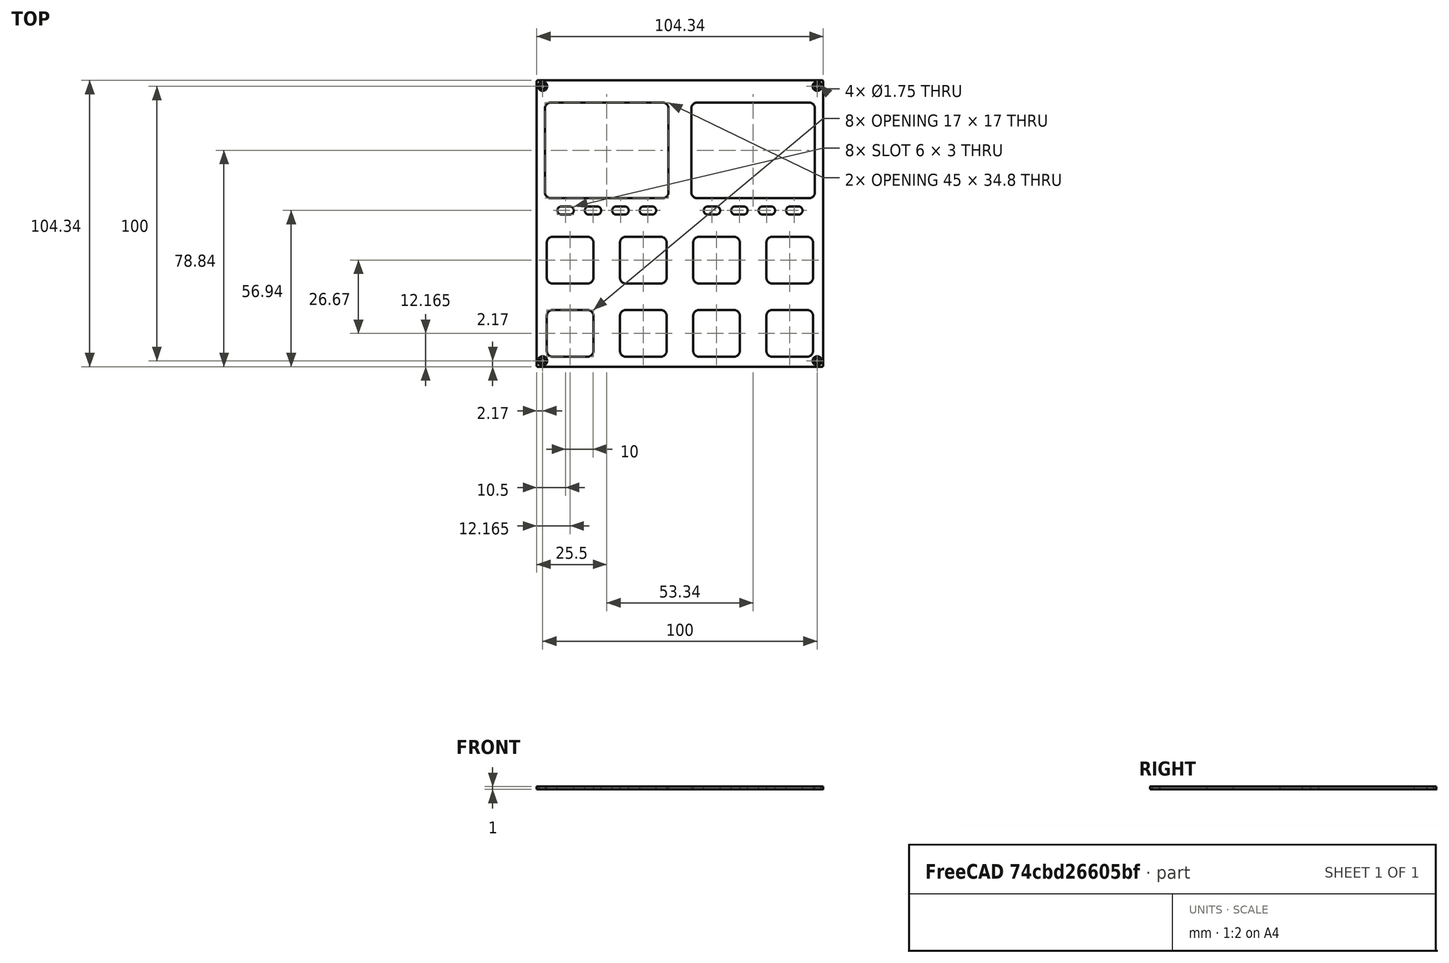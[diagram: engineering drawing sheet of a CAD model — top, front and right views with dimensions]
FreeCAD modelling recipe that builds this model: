
FCSTD DOCUMENT  (FreeCAD 0.21R33771 (Git))
Label: FRONTPANEL-SHEET-VSN2
License: All rights reserved
LicenseURL: https://en.wikipedia.org/wiki/All_rights_reserved
objects: TechDraw::DrawViewDimension×14, Sketcher::SketchObject×11, TechDraw::DrawViewBalloon×11, TechDraw::DrawHatch×11, TechDraw::DrawViewAnnotation×6, TechDraw::DrawViewPart×5, PartDesign::Pocket×4, TechDraw::DrawSVGTemplate×2, PartDesign::Body×2, TechDraw::DrawPage×2, Spreadsheet::Sheet×1, PartDesign::Pad×1, PartDesign::Hole×1, PartDesign::FeatureBase×1, TechDraw::DrawComplexSection×1
note: 47 computed .brp shape members not serialized (recipe doc carries the construction recipe); baked Part::Feature solids carry a one-line shape summary decoded from their .brp

FEATURE [TechDraw::DrawSVGTemplate] Template
  EditableTexts = COLOR=Anodized matte black - RAL code: 9004; CreationDate=2024/08/29; E.G.APPROVED=PRELIMINARY; FC-Scale=1:1; FC-Title=VSN2 - frontpanel; IntechStudioLtd.=Intech Studio Ltd.; MATERIAL=Aluminum 5052-H32; REV=01; STANDARD=ISO 2768 - m
  Height = 297
  Orientation = 1
  Template = <userpath>/Desktop/A3_LandscapeTD_MODIFIED.svg
  Width = 420
FEATURE [Spreadsheet::Sheet] Spreadsheet  label="dim"
  cells = A1='panel_length; B1(panel_length)=104.35; A2='panel_thickness; B2(panel_thickness)=1; A3='panel_radius; B3(panel_radius)==(104.35 - 103.6) / 2; A5='corner_drill_dist; B5(corner_drill_dist)=100; A6='corner_drill_dia; B6(corner_drill_dia)=1.75; A7='corner_drill_countersink; B7(corner_drill_countersink)=3.3; A9='undercut_width; B9(undercut_width)=1; A10='undercut_length; B10(undercut_length)=90; A11='undercut_offset; B11(undercut_offset)=1; A12='undercut_depth; B12(undercut_depth)=0.8; A14='ui_raster; B14(ui_raster)=26.67; A16='light_drill_dia; B16(light_drill_dia)=3; D16='old 2.9; A17='light_bore_dia; B17(light_bore_dia)=3.45; C17='check; D17='old 3.30; E17='DEPRICATED; A18='light_bore_depth; B18(light_bore_depth)=0.4; C18='check; D18='old 0.40; E18='DEPRICATED; A20='pot_drill_dia; B20(pot_drill_dia)=9.8; C20='check; D20='old 6.20; A21='pot_led_dist; B21(pot_led_dist)=8.5; B22=0; A23='but_drill_dia; B23(but_drill_dia)=9.8; A24='but_led_dist; B24(but_led_dist)=8.5; A26='fad_cutout_width; B26(fad_cutout_width)=2.1; C26='check; D26='old 1.50; A27='fad_cutout_length; B27(fad_cutout_length)=36; A28='fad_led_dist; B28(fad_led_dist)=25; A30='enc_drill_dia; B30(enc_drill_dia)=9.8; C30='check; D30='old 6.20; A31='enc_led_dist; B31(enc_led_dist)=8.5; A33='longfad_cutout_width; B33(longfad_cutout_width)=2.1; A34='longfad_cutout_length; B34(longfad_cutout_length)=66; A36='panel_chamfer; B36(panel_chamfer)=0.2; C36='UPDATE DRAWING
FEATURE [Sketcher::SketchObject] Sketch025  label="TEK2_TEKLight"
  FullyConstrained = true
  MapMode = 5
  Support = -> [XY_Plane011]
  expr: Constraints[49] = <<dim>>.light_drill_dia
  sketch-geometry (28):
    g0: Circle CenterX=-26.67 CenterY=26.67 CenterZ=0 NormalX=0 NormalY=0 NormalZ=1 AngleXU=0 Radius=5.25
    g1: Circle CenterX=26.67 CenterY=26.67 CenterZ=0 NormalX=0 NormalY=0 NormalZ=1 AngleXU=0 Radius=5.25
    g2: LineSegment StartX=-26.67 StartY=26.67 StartZ=0 EndX=0 EndY=26.67 EndZ=0
    g3: LineSegment StartX=0 StartY=26.67 StartZ=0 EndX=0 EndY=0 EndZ=0
    g4: LineSegment StartX=26.67 StartY=26.67 StartZ=0 EndX=0 EndY=26.67 EndZ=0
    g5: Circle CenterX=-26.67 CenterY=26.67 CenterZ=0 NormalX=0 NormalY=0 NormalZ=1 AngleXU=0 Radius=23
    g6: Circle CenterX=26.67 CenterY=26.67 CenterZ=0 NormalX=0 NormalY=0 NormalZ=1 AngleXU=0 Radius=23
    g7: Circle CenterX=-47.5151 CenterY=36.3902 CenterZ=0 NormalX=0 NormalY=0 NormalZ=1 AngleXU=0 Radius=1.5
    g8: Circle CenterX=-45.5105 CenterY=39.8623 CenterZ=0 NormalX=0 NormalY=0 NormalZ=1 AngleXU=0 Radius=1.5
    g9: Circle CenterX=-42.9335 CenterY=42.9335 CenterZ=0 NormalX=0 NormalY=0 NormalZ=1 AngleXU=0 Radius=1.5
    g10: Circle CenterX=-39.8623 CenterY=45.5105 CenterZ=0 NormalX=0 NormalY=0 NormalZ=1 AngleXU=0 Radius=1.5
    g11: Circle CenterX=-36.3902 CenterY=47.5151 CenterZ=0 NormalX=0 NormalY=0 NormalZ=1 AngleXU=0 Radius=1.5
    g12: Circle CenterX=5.82492 CenterY=36.3902 CenterZ=0 NormalX=0 NormalY=0 NormalZ=1 AngleXU=0 Radius=1.5
    g13: Circle CenterX=7.8295 CenterY=39.8623 CenterZ=0 NormalX=0 NormalY=0 NormalZ=1 AngleXU=0 Radius=1.5
    g14: Circle CenterX=10.4065 CenterY=42.9335 CenterZ=0 NormalX=0 NormalY=0 NormalZ=1 AngleXU=0 Radius=1.5
    g15: Circle CenterX=13.4777 CenterY=45.5105 CenterZ=0 NormalX=0 NormalY=0 NormalZ=1 AngleXU=0 Radius=1.5
    g16: Circle CenterX=16.9498 CenterY=47.5151 CenterZ=0 NormalX=0 NormalY=0 NormalZ=1 AngleXU=0 Radius=1.5
    g17: LineSegment StartX=-47.5151 StartY=36.3902 StartZ=0 EndX=5.82492 EndY=36.3902 EndZ=0
    g18: LineSegment StartX=-45.5105 StartY=39.8623 StartZ=0 EndX=7.8295 EndY=39.8623 EndZ=0
    g19: LineSegment StartX=-42.9335 StartY=42.9335 StartZ=0 EndX=10.4065 EndY=42.9335 EndZ=0
    g20: LineSegment StartX=-39.8623 StartY=45.5105 StartZ=0 EndX=13.4777 EndY=45.5105 EndZ=0
    g21: LineSegment StartX=-36.3902 StartY=47.5151 StartZ=0 EndX=16.9498 EndY=47.5151 EndZ=0
    g22: LineSegment StartX=5.82492 StartY=36.3902 StartZ=0 EndX=26.67 EndY=26.67 EndZ=0
    g23: LineSegment StartX=16.9498 StartY=47.5151 StartZ=0 EndX=26.67 EndY=26.67 EndZ=0
    g24: LineSegment StartX=5.82492 StartY=36.3902 StartZ=0 EndX=7.8295 EndY=39.8623 EndZ=0
    g25: LineSegment StartX=7.8295 StartY=39.8623 StartZ=0 EndX=10.4065 EndY=42.9335 EndZ=0
    g26: LineSegment StartX=13.4777 StartY=45.5105 StartZ=0 EndX=10.4065 EndY=42.9335 EndZ=0
    g27: LineSegment StartX=16.9498 StartY=47.5151 StartZ=0 EndX=13.4777 EndY=45.5105 EndZ=0
  constraints (69):
    c: Coincident(g2,g0)
    c: PointOnObject(g2,g-2)
    c: Coincident(g2,g3)
    c: Coincident(g3,g-1)
    c: Coincident(g4,g1)
    c: Coincident(g4,g2)
    c: Equal(g3,g2)
    c: Equal(g2,g4)
    c: Horizontal(g2)
    c: Horizontal(g4)
    c: DistanceY(g3,g3) = 26.67
    c: Equal(g0,g1)
    c: Coincident(g5,g0)
    c: Coincident(g6,g1)
    c: Equal(g6,g5)
    c: PointOnObject(g7,g5)
    c: PointOnObject(g8,g5)
    c: PointOnObject(g9,g5)
    c: PointOnObject(g10,g5)
    c: PointOnObject(g11,g5)
    c: PointOnObject(g12,g6)
    c: PointOnObject(g13,g6)
    c: PointOnObject(g14,g6)
    c: PointOnObject(g15,g6)
    c: PointOnObject(g16,g6)
    c: Equal(g7,g8)
    c: Equal(g8,g9)
    c: Equal(g9,g10)
    c: Equal(g10,g11)
    c: Equal(g11,g12)
    c: Equal(g12,g13)
    c: Equal(g13,g14)
    c: Equal(g14,g15)
    c: Equal(g15,g16)
    c: Coincident(g17,g7)
    c: Coincident(g17,g12)
    c: Coincident(g18,g8)
    c: Coincident(g18,g13)
    c: Horizontal(g18)
    c: Coincident(g19,g9)
    c: Coincident(g19,g14)
    c: Horizontal(g19)
    c: Coincident(g20,g10)
    c: Coincident(g20,g15)
    c: Horizontal(g20)
    c: Coincident(g21,g11)
    c: Horizontal(g21)
    c: Coincident(g21,g16)
    c: Horizontal(g17)
    c: Diameter(g12) = 3
    c: Coincident(g22,g12)
    c: Coincident(g22,g1)
    c: Coincident(g23,g16)
    c: Coincident(g23,g1)
    c: Angle(g22,g4) = 0.436332
    c: Angle(g-2,g23) = 0.436332
    c: Coincident(g24,g12)
    c: Coincident(g24,g13)
    c: Coincident(g25,g13)
    c: Coincident(g26,g15)
    c: Coincident(g26,g25)
    c: Coincident(g27,g16)
    c: Coincident(g27,g15)
    c: Coincident(g25,g14)
    c: Equal(g24,g25)
    c: Equal(g25,g26)
    c: Equal(g26,g27)
    c: Radius(g6) = 23
    c: Diameter(g1) = 10.5
FEATURE [Sketcher::SketchObject] Sketch024  label="TEK2_ButtonLight"
  FullyConstrained = true
  MapMode = 5
  Support = -> [XY_Plane011]
  expr: Constraints[42] = <<dim>>.but_led_dist
  sketch-geometry (17):
    g0: Circle CenterX=-40.005 CenterY=-4.835 CenterZ=0 NormalX=0 NormalY=0 NormalZ=1 AngleXU=0 Radius=2
    g1: Circle CenterX=-13.335 CenterY=-4.835 CenterZ=0 NormalX=0 NormalY=0 NormalZ=1 AngleXU=0 Radius=2
    g2: LineSegment StartX=-40.005 StartY=-4.835 StartZ=0 EndX=-13.335 EndY=-4.835 EndZ=0
    g3: Circle CenterX=13.335 CenterY=-4.835 CenterZ=0 NormalX=0 NormalY=0 NormalZ=1 AngleXU=0 Radius=2
    g4: LineSegment StartX=-13.335 StartY=-4.835 StartZ=0 EndX=13.335 EndY=-4.835 EndZ=0
    g5: Circle CenterX=40.005 CenterY=-4.835 CenterZ=0 NormalX=0 NormalY=0 NormalZ=1 AngleXU=0 Radius=2
    g6: LineSegment StartX=13.335 StartY=-4.835 StartZ=0 EndX=40.005 EndY=-4.835 EndZ=0
    g7: Circle CenterX=-40.005 CenterY=-31.505 CenterZ=0 NormalX=0 NormalY=0 NormalZ=1 AngleXU=0 Radius=2
    g8: LineSegment StartX=-40.005 StartY=-4.835 StartZ=0 EndX=-40.005 EndY=-31.505 EndZ=0
    g9: Circle CenterX=-13.335 CenterY=-31.505 CenterZ=0 NormalX=0 NormalY=0 NormalZ=1 AngleXU=0 Radius=2
    g10: LineSegment StartX=-40.005 StartY=-31.505 StartZ=0 EndX=-13.335 EndY=-31.505 EndZ=0
    g11: Circle CenterX=13.335 CenterY=-31.505 CenterZ=0 NormalX=0 NormalY=0 NormalZ=1 AngleXU=0 Radius=2
    g12: LineSegment StartX=-13.335 StartY=-31.505 StartZ=0 EndX=13.335 EndY=-31.505 EndZ=0
    g13: Circle CenterX=40.005 CenterY=-31.505 CenterZ=0 NormalX=0 NormalY=0 NormalZ=1 AngleXU=0 Radius=2
    g14: LineSegment StartX=13.335 StartY=-31.505 StartZ=0 EndX=40.005 EndY=-31.505 EndZ=0
    g15: LineSegment StartX=-13.335 StartY=-4.835 StartZ=0 EndX=-1.8e-15 EndY=8.5 EndZ=0
    g16: LineSegment StartX=-1.8e-15 StartY=8.5 StartZ=0 EndX=13.335 EndY=-4.835 EndZ=0
  constraints (43):
    c: Diameter(g0) = 4
    c: Coincident(g0,g2)
    c: Coincident(g1,g2)
    c: Coincident(g1,g4)
    c: Coincident(g3,g4)
    c: Coincident(g3,g6)
    c: Coincident(g5,g6)
    c: Coincident(g0,g8)
    c: Coincident(g7,g8)
    c: Coincident(g7,g10)
    c: Coincident(g9,g10)
    c: Coincident(g9,g12)
    c: Coincident(g11,g12)
    c: Coincident(g11,g14)
    c: Coincident(g13,g14)
    c: Horizontal(g4)
    c: Horizontal(g2)
    c: Horizontal(g6)
    c: Horizontal(g10)
    c: Horizontal(g12)
    c: Horizontal(g14)
    c: Vertical(g8)
    c: Equal(g8,g2)
    c: Equal(g2,g10)
    c: Equal(g10,g12)
    c: Equal(g12,g4)
    c: Equal(g4,g6)
    c: Equal(g6,g14)
    c: DistanceX(g4,g4) = 26.67
    c: Equal(g7,g9)
    c: Equal(g9,g11)
    c: Equal(g11,g13)
    c: Equal(g13,g5)
    c: Equal(g5,g3)
    c: Equal(g3,g1)
    c: Equal(g1,g0)
    c: Coincident(g15,g1)
    c: PointOnObject(g15,g-2)
    c: Coincident(g15,g16)
    c: Coincident(g16,g3)
    c: Equal(g16,g15)
    c: Perpendicular(g15,g16)
    c: DistanceY(g-1,g15) = 8.5
FEATURE [Sketcher::SketchObject] Sketch023  label="TEK2_ButtonHole"
  FullyConstrained = true
  MapMode = 5
  Support = -> [XY_Plane011]
  sketch-geometry (17):
    g0: Circle CenterX=-40.005 CenterY=-13.335 CenterZ=0 NormalX=0 NormalY=0 NormalZ=1 AngleXU=0 Radius=2
    g1: Circle CenterX=-13.335 CenterY=-13.335 CenterZ=0 NormalX=0 NormalY=0 NormalZ=1 AngleXU=0 Radius=2
    g2: LineSegment StartX=-40.005 StartY=-13.335 StartZ=0 EndX=-13.335 EndY=-13.335 EndZ=0
    g3: Circle CenterX=13.335 CenterY=-13.335 CenterZ=0 NormalX=0 NormalY=0 NormalZ=1 AngleXU=0 Radius=2
    g4: LineSegment StartX=-13.335 StartY=-13.335 StartZ=0 EndX=13.335 EndY=-13.335 EndZ=0
    g5: Circle CenterX=40.005 CenterY=-13.335 CenterZ=0 NormalX=0 NormalY=0 NormalZ=1 AngleXU=0 Radius=2
    g6: LineSegment StartX=13.335 StartY=-13.335 StartZ=0 EndX=40.005 EndY=-13.335 EndZ=0
    g7: Circle CenterX=-40.005 CenterY=-40.005 CenterZ=0 NormalX=0 NormalY=0 NormalZ=1 AngleXU=0 Radius=2
    g8: LineSegment StartX=-40.005 StartY=-13.335 StartZ=0 EndX=-40.005 EndY=-40.005 EndZ=0
    g9: Circle CenterX=-13.335 CenterY=-40.005 CenterZ=0 NormalX=0 NormalY=0 NormalZ=1 AngleXU=0 Radius=2
    g10: LineSegment StartX=-40.005 StartY=-40.005 StartZ=0 EndX=-13.335 EndY=-40.005 EndZ=0
    g11: Circle CenterX=13.335 CenterY=-40.005 CenterZ=0 NormalX=0 NormalY=0 NormalZ=1 AngleXU=0 Radius=2
    g12: LineSegment StartX=-13.335 StartY=-40.005 StartZ=0 EndX=13.335 EndY=-40.005 EndZ=0
    g13: Circle CenterX=40.005 CenterY=-40.005 CenterZ=0 NormalX=0 NormalY=0 NormalZ=1 AngleXU=0 Radius=2
    g14: LineSegment StartX=13.335 StartY=-40.005 StartZ=0 EndX=40.005 EndY=-40.005 EndZ=0
    g15: LineSegment StartX=0 StartY=0 StartZ=0 EndX=13.335 EndY=-13.335 EndZ=0
    g16: LineSegment StartX=0 StartY=0 StartZ=0 EndX=-13.335 EndY=-13.335 EndZ=0
  constraints (42):
    c: Diameter(g0) = 4
    c: Coincident(g0,g2)
    c: Coincident(g1,g2)
    c: Coincident(g1,g4)
    c: Coincident(g3,g4)
    c: Coincident(g3,g6)
    c: Coincident(g5,g6)
    c: Coincident(g0,g8)
    c: Coincident(g7,g8)
    c: Coincident(g7,g10)
    c: Coincident(g9,g10)
    c: Coincident(g9,g12)
    c: Coincident(g11,g12)
    c: Coincident(g11,g14)
    c: Coincident(g13,g14)
    c: Coincident(g-1,g16)
    c: Coincident(g16,g1)
    c: Coincident(g15,g3)
    c: Horizontal(g4)
    c: Horizontal(g2)
    c: Horizontal(g6)
    c: Horizontal(g10)
    c: Horizontal(g12)
    c: Horizontal(g14)
    c: Vertical(g8)
    c: Equal(g8,g2)
    c: Equal(g2,g10)
    c: Equal(g10,g12)
    c: Equal(g12,g4)
    c: Equal(g4,g6)
    c: Equal(g6,g14)
    c: DistanceX(g4,g4) = 26.67
    c: Equal(g16,g15)
    c: Coincident(g15,g16)
    c: Perpendicular(g15,g16)
    c: Equal(g7,g9)
    c: Equal(g9,g11)
    c: Equal(g11,g13)
    c: Equal(g13,g5)
    c: Equal(g5,g3)
    c: Equal(g3,g1)
    c: Equal(g1,g0)
FEATURE [Sketcher::SketchObject] Sketch001
  FullyConstrained = true
  MapMode = 5
  Support = -> [XY_Plane]
  expr: Constraints[13] = <<dim>>.corner_drill_dist
  sketch-geometry (9):
    g0: LineSegment StartX=-50 StartY=50 StartZ=0 EndX=-50 EndY=-50 EndZ=0
    g1: LineSegment StartX=-50 StartY=-50 StartZ=0 EndX=50 EndY=-50 EndZ=0
    g2: LineSegment StartX=50 StartY=-50 StartZ=0 EndX=50 EndY=50 EndZ=0
    g3: LineSegment StartX=50 StartY=50 StartZ=0 EndX=-50 EndY=50 EndZ=0
    g4: Circle CenterX=0 CenterY=0 CenterZ=0 NormalX=0 NormalY=0 NormalZ=1 AngleXU=0 Radius=70.7107
    g5: Circle CenterX=-50 CenterY=50 CenterZ=0 NormalX=0 NormalY=0 NormalZ=1 AngleXU=0 Radius=0.5
    g6: Circle CenterX=50 CenterY=50 CenterZ=0 NormalX=0 NormalY=0 NormalZ=1 AngleXU=0 Radius=0.5
    g7: Circle CenterX=50 CenterY=-50 CenterZ=0 NormalX=0 NormalY=0 NormalZ=1 AngleXU=0 Radius=0.5
    g8: Circle CenterX=-50 CenterY=-50 CenterZ=0 NormalX=0 NormalY=0 NormalZ=1 AngleXU=0 Radius=0.5
  constraints (22):
    c: Coincident(g0,g1)
    c: Coincident(g1,g2)
    c: Coincident(g2,g3)
    c: Coincident(g3,g0)
    c: Equal(g0,g1)
    c: Equal(g0,g2)
    c: Equal(g0,g3)
    c: PointOnObject(g0,g4)
    c: PointOnObject(g1,g4)
    c: PointOnObject(g2,g4)
    c: PointOnObject(g3,g4)
    c: Coincident(g4,g-1)
    c: Horizontal(g3)
    c: DistanceX(g3,g3) = 100
    c: Coincident(g5,g0)
    c: Coincident(g6,g2)
    c: Coincident(g7,g1)
    c: Coincident(g8,g0)
    c: Diameter(g8) = 1
    c: Equal(g8,g7)
    c: Equal(g8,g6)
    c: Equal(g8,g5)
FEATURE [Sketcher::SketchObject] Sketch002
  AttachmentOffset = pos=(0,0,-4.8) rot=(0,0,1;0rad)
  FullyConstrained = true
  MapMode = 5
  Placement = pos=(0,0,-4.8) rot=(0,0,1;0rad)
  Support = -> [XY_Plane]
  expr: .AttachmentOffset.Base.z = -<<dim>>.undercut_depth - 4
  expr: Constraints[91] = <<dim>>.undercut_length
  expr: Constraints[92] = <<dim>>.undercut_width
  expr: Constraints[93] = <<dim>>.panel_length / 2 - <<dim>>.undercut_offset - <<dim>>.undercut_width / 2
  sketch-geometry (40):
    g0: LineSegment StartX=-45 StartY=50.175 StartZ=0 EndX=45 EndY=50.175 EndZ=0
    g1: LineSegment StartX=-45 StartY=51.175 StartZ=0 EndX=45 EndY=51.175 EndZ=0
    g2: LineSegment StartX=-50.675 StartY=45 StartZ=0 EndX=0 EndY=0 EndZ=0
    g3: LineSegment StartX=0 StartY=0 StartZ=0 EndX=-50.675 EndY=-45 EndZ=0
    g4: LineSegment StartX=0 StartY=0 StartZ=0 EndX=-45 EndY=50.675 EndZ=0
    g5: LineSegment StartX=45 StartY=50.675 StartZ=0 EndX=0 EndY=0 EndZ=0
    g6: LineSegment StartX=0 StartY=0 StartZ=0 EndX=50.675 EndY=45 EndZ=0
    g7: LineSegment StartX=50.675 StartY=-45 StartZ=0 EndX=0 EndY=0 EndZ=0
    g8: LineSegment StartX=0 StartY=0 StartZ=0 EndX=45 EndY=-50.675 EndZ=0
    g9: LineSegment StartX=0 StartY=0 StartZ=0 EndX=-45 EndY=-50.675 EndZ=0
    g10: ArcOfCircle CenterX=45 CenterY=50.675 CenterZ=0 NormalX=0 NormalY=0 NormalZ=1 AngleXU=0 Radius=0.5 StartAngle=4.71239 EndAngle=6.28319
    g11: ArcOfCircle CenterX=45 CenterY=50.675 CenterZ=0 NormalX=0 NormalY=0 NormalZ=1 AngleXU=0 Radius=0.5 StartAngle=0 EndAngle=1.5708
    g12: LineSegment StartX=45 StartY=50.675 StartZ=0 EndX=45.5 EndY=50.675 EndZ=0
    g13: ArcOfCircle CenterX=-45 CenterY=50.675 CenterZ=0 NormalX=0 NormalY=0 NormalZ=1 AngleXU=0 Radius=0.5 StartAngle=3.14159 EndAngle=4.71239
    g14: ArcOfCircle CenterX=-45 CenterY=50.675 CenterZ=0 NormalX=0 NormalY=0 NormalZ=1 AngleXU=0 Radius=0.5 StartAngle=1.5708 EndAngle=3.14159
    g15: LineSegment StartX=-45.5 StartY=50.675 StartZ=0 EndX=-45 EndY=50.675 EndZ=0
    g16: LineSegment StartX=-45 StartY=-51.175 StartZ=0 EndX=45 EndY=-51.175 EndZ=0
    g17: LineSegment StartX=-45 StartY=-50.175 StartZ=0 EndX=45 EndY=-50.175 EndZ=0
    g18: ArcOfCircle CenterX=45 CenterY=-50.675 CenterZ=0 NormalX=0 NormalY=0 NormalZ=1 AngleXU=0 Radius=0.5 StartAngle=4.71239 EndAngle=6.28319
    g19: ArcOfCircle CenterX=45 CenterY=-50.675 CenterZ=0 NormalX=0 NormalY=0 NormalZ=1 AngleXU=0 Radius=0.5 StartAngle=0 EndAngle=1.5708
    g20: LineSegment StartX=45 StartY=-50.675 StartZ=0 EndX=45.5 EndY=-50.675 EndZ=0
    g21: ArcOfCircle CenterX=-45 CenterY=-50.675 CenterZ=0 NormalX=0 NormalY=0 NormalZ=1 AngleXU=0 Radius=0.5 StartAngle=3.14159 EndAngle=4.71239
    g22: ArcOfCircle CenterX=-45 CenterY=-50.675 CenterZ=0 NormalX=0 NormalY=0 NormalZ=1 AngleXU=0 Radius=0.5 StartAngle=1.5708 EndAngle=3.14159
    g23: LineSegment StartX=-45.5 StartY=-50.675 StartZ=0 EndX=-45 EndY=-50.675 EndZ=0
    g24: LineSegment StartX=51.175 StartY=-45 StartZ=0 EndX=51.175 EndY=45 EndZ=0
    g25: LineSegment StartX=50.175 StartY=-45 StartZ=0 EndX=50.175 EndY=45 EndZ=0
    g26: ArcOfCircle CenterX=50.675 CenterY=45 CenterZ=0 NormalX=0 NormalY=0 NormalZ=1 AngleXU=0 Radius=0.5 StartAngle=3.8e-15 EndAngle=1.5708
    g27: ArcOfCircle CenterX=50.675 CenterY=45 CenterZ=0 NormalX=0 NormalY=0 NormalZ=1 AngleXU=0 Radius=0.5 StartAngle=1.5708 EndAngle=3.14159
    g28: LineSegment StartX=50.675 StartY=45 StartZ=0 EndX=50.675 EndY=45.5 EndZ=0
    g29: ArcOfCircle CenterX=50.675 CenterY=-45 CenterZ=0 NormalX=0 NormalY=0 NormalZ=1 AngleXU=0 Radius=0.5 StartAngle=4.71239 EndAngle=6.28319
    g30: ArcOfCircle CenterX=50.675 CenterY=-45 CenterZ=0 NormalX=0 NormalY=0 NormalZ=1 AngleXU=0 Radius=0.5 StartAngle=3.14159 EndAngle=4.71239
    g31: LineSegment StartX=50.675 StartY=-45.5 StartZ=0 EndX=50.675 EndY=-45 EndZ=0
    g32: LineSegment StartX=-50.175 StartY=-45 StartZ=0 EndX=-50.175 EndY=45 EndZ=0
    g33: LineSegment StartX=-51.175 StartY=-45 StartZ=0 EndX=-51.175 EndY=45 EndZ=0
    g34: ArcOfCircle CenterX=-50.675 CenterY=45 CenterZ=0 NormalX=0 NormalY=0 NormalZ=1 AngleXU=0 Radius=0.5 StartAngle=1.4e-15 EndAngle=1.5708
    g35: ArcOfCircle CenterX=-50.675 CenterY=45 CenterZ=0 NormalX=0 NormalY=0 NormalZ=1 AngleXU=0 Radius=0.5 StartAngle=1.5708 EndAngle=3.14159
    g36: LineSegment StartX=-50.675 StartY=45 StartZ=0 EndX=-50.675 EndY=45.5 EndZ=0
    g37: ArcOfCircle CenterX=-50.675 CenterY=-45 CenterZ=0 NormalX=0 NormalY=0 NormalZ=1 AngleXU=0 Radius=0.5 StartAngle=4.71239 EndAngle=6.28319
    g38: ArcOfCircle CenterX=-50.675 CenterY=-45 CenterZ=0 NormalX=0 NormalY=0 NormalZ=1 AngleXU=0 Radius=0.5 StartAngle=3.14159 EndAngle=4.71239
    g39: LineSegment StartX=-50.675 StartY=-45.5 StartZ=0 EndX=-50.675 EndY=-45 EndZ=0
  constraints (96):
    c: Horizontal(g0)
    c: Coincident(g2,g-1)
    c: Coincident(g2,g3)
    c: Coincident(g-1,g4)
    c: Coincident(g5,g-1)
    c: Coincident(g5,g6)
    c: Coincident(g7,g-1)
    c: Coincident(g7,g8)
    c: Coincident(g-1,g9)
    c: Equal(g5,g6)
    c: Equal(g6,g8)
    c: Equal(g8,g7)
    c: Equal(g7,g9)
    c: Equal(g9,g3)
    c: Equal(g3,g2)
    c: Equal(g2,g4)
    c: Coincident(g10,g5)
    c: Coincident(g11,g10)
    c: Coincident(g11,g10)
    c: Tangent(g11,g1) = 1.5708
    c: Tangent(g10,g0) = -1.5708
    c: Coincident(g12,g10)
    c: Coincident(g12,g10)
    c: Horizontal(g12)
    c: Coincident(g13,g4)
    c: Coincident(g14,g13)
    c: Coincident(g14,g13)
    c: Tangent(g14,g1) = 1.5708
    c: Tangent(g13,g0) = -1.5708
    c: Coincident(g15,g13)
    c: Coincident(g15,g13)
    c: Horizontal(g15)
    c: Horizontal(g1)
    c: Horizontal(g16)
    c: Coincident(g19,g18)
    c: Coincident(g19,g18)
    c: Tangent(g19,g17) = 1.5708
    c: Tangent(g18,g16) = -1.5708
    c: Coincident(g20,g18)
    c: Coincident(g20,g18)
    c: Horizontal(g20)
    c: Coincident(g22,g21)
    c: Coincident(g22,g21)
    c: Tangent(g22,g17) = 1.5708
    c: Tangent(g21,g16) = -1.5708
    c: Coincident(g23,g21)
    c: Coincident(g23,g21)
    c: Horizontal(g23)
    c: Horizontal(g17)
    c: Coincident(g21,g9)
    c: Coincident(g8,g18)
    c: Equal(g22,g14)
    c: Equal(g17,g1)
    c: Coincident(g27,g26)
    c: Coincident(g27,g26)
    c: Tangent(g27,g25) = 1.5708
    c: Tangent(g26,g24) = -1.5708
    c: Coincident(g28,g26)
    c: Coincident(g28,g26)
    c: Coincident(g30,g29)
    c: Coincident(g30,g29)
    c: Tangent(g30,g25) = 1.5708
    c: Tangent(g29,g24) = -1.5708
    c: Coincident(g31,g29)
    c: Coincident(g31,g29)
    c: Vertical(g31)
    c: Vertical(g28)
    c: Vertical(g25)
    c: Vertical(g24)
    c: Coincident(g35,g34)
    c: Coincident(g35,g34)
    c: Tangent(g35,g33) = 1.5708
    c: Tangent(g34,g32) = -1.5708
    c: Coincident(g36,g34)
    c: Coincident(g36,g34)
    c: Coincident(g38,g37)
    c: Coincident(g38,g37)
    c: Tangent(g38,g33) = 1.5708
    c: Tangent(g37,g32) = -1.5708
    c: Coincident(g39,g37)
    c: Coincident(g39,g37)
    c: Vertical(g39)
    c: Vertical(g36)
    c: Vertical(g33)
    c: Vertical(g32)
    c: Coincident(g6,g26)
    c: Coincident(g7,g29)
    c: Equal(g25,g0)
    c: Equal(g11,g27)
    c: Equal(g1,g33)
    c: Equal(g35,g11)
    c: DistanceX(g13,g10) = 90
    c: Diameter(g13) = 1
    c: DistanceY(g-1,g13) = 50.675
    c: Coincident(g2,g34)
    c: Coincident(g3,g37)
FEATURE [Sketcher::SketchObject] Sketch
  FullyConstrained = true
  MapMode = 5
  Support = -> [XY_Plane]
  expr: Constraints[12] = <<dim>>.panel_radius
  expr: Constraints[16] = <<dim>>.panel_length
  sketch-geometry (11):
    g0: LineSegment StartX=-51.8 StartY=52.175 StartZ=0 EndX=51.8 EndY=52.175 EndZ=0
    g1: LineSegment StartX=52.175 StartY=51.8 StartZ=0 EndX=52.175 EndY=-51.8 EndZ=0
    g2: LineSegment StartX=51.8 StartY=-52.175 StartZ=0 EndX=-51.8 EndY=-52.175 EndZ=0
    g3: LineSegment StartX=-52.175 StartY=-51.8 StartZ=0 EndX=-52.175 EndY=51.8 EndZ=0
    g4: ArcOfCircle CenterX=-51.8 CenterY=51.8 CenterZ=0 NormalX=0 NormalY=0 NormalZ=1 AngleXU=0 Radius=0.375 StartAngle=1.5708 EndAngle=3.14159
    g5: ArcOfCircle CenterX=51.8 CenterY=51.8 CenterZ=0 NormalX=0 NormalY=0 NormalZ=1 AngleXU=0 Radius=0.375 StartAngle=8.4e-15 EndAngle=1.5708
    g6: ArcOfCircle CenterX=51.8 CenterY=-51.8 CenterZ=0 NormalX=0 NormalY=0 NormalZ=1 AngleXU=0 Radius=0.375 StartAngle=4.71239 EndAngle=6.28319
    g7: ArcOfCircle CenterX=-51.8 CenterY=-51.8 CenterZ=0 NormalX=0 NormalY=0 NormalZ=1 AngleXU=0 Radius=0.375 StartAngle=3.14159 EndAngle=4.71239
    g8: LineSegment StartX=-51.8 StartY=51.8 StartZ=0 EndX=0 EndY=0 EndZ=0
    g9: LineSegment StartX=0 StartY=0 StartZ=0 EndX=51.8 EndY=51.8 EndZ=0
    g10: LineSegment StartX=0 StartY=0 StartZ=0 EndX=-51.8 EndY=-51.8 EndZ=0
  constraints (26):
    c: Horizontal(g0)
    c: Horizontal(g2)
    c: Vertical(g1)
    c: Vertical(g3)
    c: Tangent(g3,g4) = 1.5708
    c: Tangent(g0,g4) = 1.5708
    c: Tangent(g0,g5) = 1.5708
    c: Tangent(g1,g5) = 1.5708
    c: Tangent(g1,g6) = 1.5708
    c: Tangent(g2,g6) = 1.5708
    c: Tangent(g2,g7) = 1.5708
    c: Tangent(g3,g7) = 1.5708
    c: Radius(g4) = 0.375
    c: Equal(g4,g5)
    c: Equal(g4,g6)
    c: Equal(g4,g7)
    c: DistanceX(g3,g1) = 104.35
    c: Equal(g3,g0)
    c: Coincident(g8,g4)
    c: Coincident(g8,g-1)
    c: Coincident(g8,g9)
    c: Coincident(g9,g5)
    c: Coincident(g-1,g10)
    c: Coincident(g10,g7)
    c: Equal(g10,g8)
    c: Equal(g8,g9)
FEATURE [PartDesign::Pad] Pad  label="panel"
  AllowMultiFace = false
  Direction = (0,0,1)
  Length = 1
  Length2 = 100
  Profile = -> Sketch
  Reversed = true
  Type = 0
  expr: Length = <<dim>>.panel_thickness
FEATURE [PartDesign::Pocket] Pocket
  AllowMultiFace = false
  BaseFeature = -> Pad
  Direction = (0,0,-1)
  Length = 5
  Length2 = 100
  Profile = -> Sketch002
  Type = 1
FEATURE [PartDesign::Hole] Hole
  BaseFeature = -> Pocket
  CustomThreadClearance = 0
  Depth = 298.105
  DepthType = 1
  Diameter = 1.75
  DrillForDepth = false
  DrillPoint = 1
  DrillPointAngle = 118
  HoleCutCountersinkAngle = 90
  HoleCutCustomValues = false
  HoleCutDepth = 0
  HoleCutDiameter = 3.3
  HoleCutType = 2
  ModelThread = false
  Profile = -> Sketch001
  Tapered = false
  TaperedAngle = 90
  ThreadClass = 0
  ThreadDepth = 298.105
  ThreadDepthType = 0
  ThreadDirection = 0
  ThreadFit = 0
  ThreadSize = 0
  ThreadType = 0
  Threaded = false
  UseCustomThreadClearance = false
  expr: Diameter = <<dim>>.corner_drill_dia
  expr: HoleCutDiameter = <<dim>>.corner_drill_countersink
FEATURE [PartDesign::Body] Body  label="Base"
  Group = -> [Sketch,Pad,Sketch001,Sketch002,Pocket,Hole]
  Origin = -> Origin
  Tip = -> Hole
FEATURE [PartDesign::FeatureBase] Clone009
  BaseFeature = -> Body
FEATURE [Sketcher::SketchObject] Sketch026  label="Section A-A"
  FullyConstrained = true
  MapMode = 5
  Support = -> [XY_Plane011]
  sketch-geometry (1):
    g0: LineSegment StartX=-53.5 StartY=-50 StartZ=0 EndX=-46.5 EndY=-50 EndZ=0
  constraints (4):
    c: Horizontal(g0)
    c: DistanceX(g0,g0) = 7
    c: DistanceY(g0,g-1) = 50
    c: DistanceX(g0,g-1) = 46.5
FEATURE [TechDraw::DrawViewAnnotation] Annotation
  Font = osifont
  LineSpace = 100
  LockPosition = false
  MaxWidth = -1
  Rotation = 0
  ScaleType = 0
  Text = 10:1
  TextSize = 4
  TextStyle = 0
  X = 288.818
  Y = 78.3445
FEATURE [TechDraw::DrawViewAnnotation] Annotation001
  Font = osifont
  LineSpace = 100
  LockPosition = false
  MaxWidth = -1
  Rotation = 0
  ScaleType = 0
  Text = 1:2
  TextSize = 4
  TextStyle = 0
  X = 191.608
  Y = 62.7873
FEATURE [Sketcher::SketchObject] Sketch027
  FullyConstrained = false
  MapMode = 5
  Support = -> [XY_Plane011]
  sketch-geometry (20):
    g0: LineSegment StartX=-49.17 StartY=11.27 StartZ=0 EndX=-49.17 EndY=42.07 EndZ=0
    g1: LineSegment StartX=-47.17 StartY=44.07 StartZ=0 EndX=-6.17 EndY=44.07 EndZ=0
    g2: LineSegment StartX=-4.17 StartY=42.07 StartZ=0 EndX=-4.17 EndY=11.27 EndZ=0
    g3: LineSegment StartX=-6.17 StartY=9.27 StartZ=0 EndX=-47.17 EndY=9.27 EndZ=0
    g4: GeomPoint X=-26.67 Y=26.67 Z=0
    g5: ArcOfCircle CenterX=-47.17 CenterY=42.07 CenterZ=0 NormalX=0 NormalY=0 NormalZ=1 AngleXU=0 Radius=2 StartAngle=1.5708 EndAngle=3.14159
    g6: ArcOfCircle CenterX=-6.17 CenterY=42.07 CenterZ=0 NormalX=0 NormalY=0 NormalZ=1 AngleXU=0 Radius=2 StartAngle=-1.8e-15 EndAngle=1.5708
    g7: ArcOfCircle CenterX=-6.17 CenterY=11.27 CenterZ=0 NormalX=0 NormalY=0 NormalZ=1 AngleXU=0 Radius=2 StartAngle=4.71239 EndAngle=6.28319
    g8: ArcOfCircle CenterX=-47.17 CenterY=11.27 CenterZ=0 NormalX=0 NormalY=0 NormalZ=1 AngleXU=0 Radius=2 StartAngle=3.14159 EndAngle=4.71239
    g9: LineSegment StartX=-26.67 StartY=44.07 StartZ=0 EndX=-26.67 EndY=9.27 EndZ=0
    g10: LineSegment StartX=-49.17 StartY=26.67 StartZ=0 EndX=-4.17 EndY=26.67 EndZ=0
    g11: LineSegment StartX=4.17 StartY=11.27 StartZ=0 EndX=4.17 EndY=42.07 EndZ=0
    g12: LineSegment StartX=6.17 StartY=44.07 StartZ=0 EndX=47.17 EndY=44.07 EndZ=0
    g13: LineSegment StartX=49.17 StartY=42.07 StartZ=0 EndX=49.17 EndY=11.27 EndZ=0
    g14: LineSegment StartX=47.17 StartY=9.27 StartZ=0 EndX=6.17 EndY=9.27 EndZ=0
    g15: GeomPoint X=26.5959 Y=26.67 Z=0
    g16: ArcOfCircle CenterX=6.17 CenterY=42.07 CenterZ=0 NormalX=0 NormalY=0 NormalZ=1 AngleXU=0 Radius=2 StartAngle=1.5708 EndAngle=3.14159
    g17: ArcOfCircle CenterX=47.17 CenterY=42.07 CenterZ=0 NormalX=0 NormalY=0 NormalZ=1 AngleXU=0 Radius=2 StartAngle=-9e-16 EndAngle=1.5708
    g18: ArcOfCircle CenterX=47.17 CenterY=11.27 CenterZ=0 NormalX=0 NormalY=0 NormalZ=1 AngleXU=0 Radius=2 StartAngle=4.71239 EndAngle=6.28319
    g19: ArcOfCircle CenterX=6.17 CenterY=11.27 CenterZ=0 NormalX=0 NormalY=0 NormalZ=1 AngleXU=0 Radius=2 StartAngle=3.14159 EndAngle=4.71239
  constraints (49):
    c: Horizontal(g1)
    c: Horizontal(g3)
    c: Vertical(g0)
    c: Vertical(g2)
    c: DistanceY(g-1,g4) = 26.67
    c: Tangent(g1,g5) = 1.5708
    c: Tangent(g0,g5) = 1.5708
    c: Tangent(g1,g6) = 1.5708
    c: Tangent(g2,g6) = 1.5708
    c: Tangent(g2,g7) = 1.5708
    c: Tangent(g3,g7) = 1.5708
    c: Tangent(g3,g8) = 1.5708
    c: Tangent(g0,g8) = 1.5708
    c: Equal(g5,g6)
    c: Equal(g6,g7)
    c: Equal(g7,g8)
    c: DistanceX(g0,g2) = 45
    c: DistanceY(g3,g1) = 34.8
    c: PointOnObject(g9,g3)
    c: Vertical(g9)
    c: PointOnObject(g10,g0)
    c: Horizontal(g10)
    c: Symmetric(g2,g2,g10)
    c: Symmetric(g1,g1,g9)
    c: PointOnObject(g4,g9)
    c: PointOnObject(g4,g10)
    c: Diameter(g6) = 4
    c: DistanceX(g4,g-1) = 26.67
    c: DistanceY(g-1,g3) = 9.27
    c: Horizontal(g12)
    c: Horizontal(g14)
    c: Vertical(g11)
    c: Vertical(g13)
    c: Horizontal(g15,g4)
    c: Tangent(g12,g16) = 1.5708
    c: Tangent(g11,g16) = 1.5708
    c: Tangent(g12,g17) = 1.5708
    c: Tangent(g13,g17) = 1.5708
    c: Tangent(g13,g18) = 1.5708
    c: Tangent(g14,g18) = 1.5708
    c: Tangent(g11,g19) = 1.5708
    c: Tangent(g14,g19) = 1.5708
    c: Equal(g16,g17)
    c: Equal(g17,g18)
    c: Equal(g18,g19)
    c: Equal(g19,g7)
    c: Equal(g11,g2)
    c: Symmetric(g3,g14,g-2)
    c: Equal(g14,g3)
FEATURE [PartDesign::Pocket] Pocket008  label="TEK1_display"
  BaseFeature = -> Clone009
  Direction = (0,0,-1)
  Length = 5
  Length2 = 5
  Profile = -> Sketch027
  ReferenceAxis = -> Sketch027 [N_Axis]
  Type = 1
FEATURE [Sketcher::SketchObject] Sketch028  label="LocatorPin"
  FullyConstrained = true
  MapMode = 5
  Support = -> [XY_Plane011]
  sketch-geometry (3):
    g0: Circle CenterX=-48.77 CenterY=8.17 CenterZ=0 NormalX=0 NormalY=0 NormalZ=1 AngleXU=0 Radius=0.6
    g1: Circle CenterX=-4.57 CenterY=45.17 CenterZ=0 NormalX=0 NormalY=0 NormalZ=1 AngleXU=0 Radius=0.6
    g2: GeomPoint X=-26.67 Y=26.67 Z=0
  constraints (8):
    c: Equal(g1,g0)
    c: Diameter(g1) = 1.2
    c: DistanceX(g2,g-1) = 26.67
    c: DistanceY(g-1,g2) = 26.67
    c: DistanceX(g0,g2) = 22.1
    c: DistanceY(g0,g2) = 18.5
    c: DistanceX(g2,g1) = 22.1
    c: DistanceY(g2,g1) = 18.5
FEATURE [Sketcher::SketchObject] Sketch029
  FullyConstrained = true
  MapMode = 5
  Support = -> [XY_Plane011]
  sketch-geometry (61):
    g0: LineSegment StartX=-47.07 StartY=4.77 StartZ=0 EndX=-6.27 EndY=4.77 EndZ=0
    g1: GeomPoint X=-26.67 Y=4.77 Z=0
    g2: LineSegment StartX=-34.67 StartY=3.12 StartZ=0 EndX=-34.67 EndY=6.42 EndZ=0
    g3: LineSegment StartX=-34.67 StartY=6.42 StartZ=0 EndX=-28.67 EndY=6.42 EndZ=0
    g4: LineSegment StartX=-28.67 StartY=6.42 StartZ=0 EndX=-28.67 EndY=3.12 EndZ=0
    g5: LineSegment StartX=-28.67 StartY=3.12 StartZ=0 EndX=-34.67 EndY=3.12 EndZ=0
    g6: GeomPoint X=-31.67 Y=4.77 Z=0
    g7: LineSegment StartX=-44.67 StartY=3.12 StartZ=0 EndX=-44.67 EndY=6.42 EndZ=0
    g8: LineSegment StartX=-44.67 StartY=6.42 StartZ=0 EndX=-38.67 EndY=6.42 EndZ=0
    g9: LineSegment StartX=-38.67 StartY=6.42 StartZ=0 EndX=-38.67 EndY=3.12 EndZ=0
    g10: LineSegment StartX=-38.67 StartY=3.12 StartZ=0 EndX=-44.67 EndY=3.12 EndZ=0
    g11: GeomPoint X=-41.67 Y=4.77 Z=0
    g12: LineSegment StartX=-24.67 StartY=3.12 StartZ=0 EndX=-24.67 EndY=6.42 EndZ=0
    g13: LineSegment StartX=-24.67 StartY=6.42 StartZ=0 EndX=-18.67 EndY=6.42 EndZ=0
    g14: LineSegment StartX=-18.67 StartY=6.42 StartZ=0 EndX=-18.67 EndY=3.12 EndZ=0
    g15: LineSegment StartX=-18.67 StartY=3.12 StartZ=0 EndX=-24.67 EndY=3.12 EndZ=0
    g16: GeomPoint X=-21.67 Y=4.77 Z=0
    g17: LineSegment StartX=-14.67 StartY=3.12 StartZ=0 EndX=-14.67 EndY=6.42 EndZ=0
    g18: LineSegment StartX=-14.67 StartY=6.42 StartZ=0 EndX=-8.67 EndY=6.42 EndZ=0
    g19: LineSegment StartX=-8.67 StartY=6.42 StartZ=0 EndX=-8.67 EndY=3.12 EndZ=0
    g20: LineSegment StartX=-8.67 StartY=3.12 StartZ=0 EndX=-14.67 EndY=3.12 EndZ=0
    g21: GeomPoint X=-11.67 Y=4.77 Z=0
    g22: ArcOfCircle CenterX=-33.17 CenterY=4.77 CenterZ=0 NormalX=0 NormalY=0 NormalZ=1 AngleXU=0 Radius=1.5 StartAngle=1.5708 EndAngle=4.71239
    g23: ArcOfCircle CenterX=-30.17 CenterY=4.77 CenterZ=0 NormalX=0 NormalY=0 NormalZ=1 AngleXU=0 Radius=1.5 StartAngle=4.71239 EndAngle=7.85398
    g24: LineSegment StartX=-33.17 StartY=3.27 StartZ=0 EndX=-30.17 EndY=3.27 EndZ=0
    g25: LineSegment StartX=-30.17 StartY=6.27 StartZ=0 EndX=-33.17 EndY=6.27 EndZ=0
    g26: ArcOfCircle CenterX=-23.17 CenterY=4.77 CenterZ=0 NormalX=0 NormalY=0 NormalZ=1 AngleXU=0 Radius=1.5 StartAngle=1.5708 EndAngle=4.71239
    g27: ArcOfCircle CenterX=-20.17 CenterY=4.77 CenterZ=0 NormalX=0 NormalY=0 NormalZ=1 AngleXU=0 Radius=1.5 StartAngle=4.71239 EndAngle=7.85398
    g28: LineSegment StartX=-23.17 StartY=3.27 StartZ=0 EndX=-20.17 EndY=3.27 EndZ=0
    g29: LineSegment StartX=-20.17 StartY=6.27 StartZ=0 EndX=-23.17 EndY=6.27 EndZ=0
    g30: ArcOfCircle CenterX=-13.17 CenterY=4.77 CenterZ=0 NormalX=0 NormalY=0 NormalZ=1 AngleXU=0 Radius=1.5 StartAngle=1.5708 EndAngle=4.71239
    g31: ArcOfCircle CenterX=-10.17 CenterY=4.77 CenterZ=0 NormalX=0 NormalY=0 NormalZ=1 AngleXU=0 Radius=1.5 StartAngle=4.71239 EndAngle=7.85398
    g32: LineSegment StartX=-13.17 StartY=3.27 StartZ=0 EndX=-10.17 EndY=3.27 EndZ=0
    g33: LineSegment StartX=-10.17 StartY=6.27 StartZ=0 EndX=-13.17 EndY=6.27 EndZ=0
    g34: ArcOfCircle CenterX=-43.17 CenterY=4.77 CenterZ=0 NormalX=0 NormalY=0 NormalZ=1 AngleXU=0 Radius=1.5 StartAngle=1.5708 EndAngle=4.71239
    g35: ArcOfCircle CenterX=-40.17 CenterY=4.77 CenterZ=0 NormalX=0 NormalY=0 NormalZ=1 AngleXU=0 Radius=1.5 StartAngle=4.71239 EndAngle=7.85398
    g36: LineSegment StartX=-43.17 StartY=3.27 StartZ=0 EndX=-40.17 EndY=3.27 EndZ=0
    g37: LineSegment StartX=-40.17 StartY=6.27 StartZ=0 EndX=-43.17 EndY=6.27 EndZ=0
    g38: GeomPoint X=-26.67 Y=11.37 Z=0
    g39: LineSegment StartX=6.27 StartY=4.77 StartZ=0 EndX=47.07 EndY=4.77 EndZ=0
    g40: ArcOfCircle CenterX=10.17 CenterY=4.77 CenterZ=0 NormalX=0 NormalY=0 NormalZ=1 AngleXU=0 Radius=1.5 StartAngle=1.5708 EndAngle=4.71239
    g41: ArcOfCircle CenterX=13.17 CenterY=4.77 CenterZ=0 NormalX=0 NormalY=0 NormalZ=1 AngleXU=0 Radius=1.5 StartAngle=4.71239 EndAngle=7.85398
    g42: LineSegment StartX=10.17 StartY=3.27 StartZ=0 EndX=13.17 EndY=3.27 EndZ=0
    g43: LineSegment StartX=13.17 StartY=6.27 StartZ=0 EndX=10.17 EndY=6.27 EndZ=0
    g44: ArcOfCircle CenterX=20.17 CenterY=4.77 CenterZ=0 NormalX=0 NormalY=0 NormalZ=1 AngleXU=0 Radius=1.5 StartAngle=1.5708 EndAngle=4.71239
    g45: ArcOfCircle CenterX=23.17 CenterY=4.77 CenterZ=0 NormalX=0 NormalY=0 NormalZ=1 AngleXU=0 Radius=1.5 StartAngle=4.71239 EndAngle=7.85398
    g46: LineSegment StartX=20.17 StartY=3.27 StartZ=0 EndX=23.17 EndY=3.27 EndZ=0
    g47: LineSegment StartX=23.17 StartY=6.27 StartZ=0 EndX=20.17 EndY=6.27 EndZ=0
    g48: ArcOfCircle CenterX=30.17 CenterY=4.77 CenterZ=0 NormalX=0 NormalY=0 NormalZ=1 AngleXU=0 Radius=1.5 StartAngle=1.5708 EndAngle=4.71239
    g49: ArcOfCircle CenterX=33.17 CenterY=4.77 CenterZ=0 NormalX=0 NormalY=0 NormalZ=1 AngleXU=0 Radius=1.5 StartAngle=4.71239 EndAngle=7.85398
    g50: LineSegment StartX=30.17 StartY=3.27 StartZ=0 EndX=33.17 EndY=3.27 EndZ=0
    g51: LineSegment StartX=33.17 StartY=6.27 StartZ=0 EndX=30.17 EndY=6.27 EndZ=0
    g52: ArcOfCircle CenterX=40.17 CenterY=4.77 CenterZ=0 NormalX=0 NormalY=0 NormalZ=1 AngleXU=0 Radius=1.5 StartAngle=1.5708 EndAngle=4.71239
    g53: ArcOfCircle CenterX=43.17 CenterY=4.77 CenterZ=0 NormalX=0 NormalY=0 NormalZ=1 AngleXU=0 Radius=1.5 StartAngle=4.71239 EndAngle=7.85398
    g54: LineSegment StartX=40.17 StartY=3.27 StartZ=0 EndX=43.17 EndY=3.27 EndZ=0
    g55: LineSegment StartX=43.17 StartY=6.27 StartZ=0 EndX=40.17 EndY=6.27 EndZ=0
    g56: GeomPoint X=26.67 Y=4.77 Z=0
    g57: GeomPoint X=11.67 Y=4.77 Z=0
    g58: GeomPoint X=21.67 Y=4.77 Z=0
    g59: GeomPoint X=31.67 Y=4.77 Z=0
    g60: GeomPoint X=41.67 Y=4.77 Z=0
  constraints (140):
    c: Horizontal(g0)
    c: DistanceX(g0,g0) = 40.8
    c: Symmetric(g0,g0,g1)
    c: DistanceX(g1,g-1) = 26.67
    c: Coincident(g2,g3)
    c: Coincident(g3,g4)
    c: Coincident(g4,g5)
    c: Coincident(g5,g2)
    c: Horizontal(g3)
    c: Horizontal(g5)
    c: Vertical(g2)
    c: Vertical(g4)
    c: Symmetric(g3,g2,g6)
    c: PointOnObject(g6,g0)
    c: Coincident(g7,g8)
    c: Coincident(g8,g9)
    c: Coincident(g9,g10)
    c: Coincident(g10,g7)
    c: Horizontal(g8)
    c: Horizontal(g10)
    c: Vertical(g7)
    c: Vertical(g9)
    c: Symmetric(g8,g7,g11)
    c: PointOnObject(g11,g0)
    c: Coincident(g12,g13)
    c: Coincident(g13,g14)
    c: Coincident(g14,g15)
    c: Coincident(g15,g12)
    c: Horizontal(g13)
    c: Horizontal(g15)
    c: Vertical(g12)
    c: Vertical(g14)
    c: Symmetric(g13,g12,g16)
    c: Coincident(g17,g18)
    c: Coincident(g18,g19)
    c: Coincident(g19,g20)
    c: Coincident(g20,g17)
    c: Horizontal(g18)
    c: Horizontal(g20)
    c: Vertical(g17)
    c: Vertical(g19)
    c: Symmetric(g18,g17,g21)
    c: Symmetric(g16,g6,g1)
    c: Symmetric(g11,g21,g1)
    c: Equal(g13,g3)
    c: Equal(g3,g8)
    c: Equal(g8,g18)
    c: Equal(g14,g17)
    c: Equal(g17,g4)
    c: Equal(g4,g9)
    c: DistanceX(g13,g13) = 6
    c: DistanceY(g19,g19) = 3.3
    c: Tangent(g22,g24) = -1.5708
    c: Tangent(g24,g23) = -1.5708
    c: Tangent(g23,g25) = -1.5708
    c: Tangent(g25,g22) = -1.5708
    c: Equal(g22,g23)
    c: PointOnObject(g22,g0)
    c: Tangent(g26,g28) = -1.5708
    c: Tangent(g28,g27) = -1.5708
    c: Tangent(g27,g29) = -1.5708
    c: Tangent(g29,g26) = -1.5708
    c: Equal(g26,g27)
    c: PointOnObject(g26,g0)
    c: Tangent(g30,g32) = -1.5708
    c: Tangent(g32,g31) = -1.5708
    c: Tangent(g31,g33) = -1.5708
    c: Tangent(g33,g30) = -1.5708
    c: Equal(g30,g31)
    c: PointOnObject(g30,g0)
    c: Tangent(g34,g36) = -1.5708
    c: Tangent(g36,g35) = -1.5708
    c: Tangent(g35,g37) = -1.5708
    c: Tangent(g37,g34) = -1.5708
    c: Equal(g34,g35)
    c: PointOnObject(g34,g0)
    c: Equal(g35,g23)
    c: Equal(g23,g27)
    c: Equal(g27,g31)
    c: Equal(g29,g33)
    c: Equal(g33,g25)
    c: Equal(g25,g37)
    c: Symmetric(g34,g35,g11)
    c: Symmetric(g22,g23,g6)
    c: Symmetric(g26,g27,g16)
    c: Symmetric(g30,g31,g21)
    c: Diameter(g31) = 3
    c: DistanceX(g33,g33) = 3
    c: DistanceY(g-1,g38) = 11.37
    c: Vertical(g38,g1)
    c: DistanceY(g23,g38) = 5.1
    c: DistanceY(g-1,g0) = 4.77
    c: Horizontal(g39)
    c: Tangent(g40,g42) = -1.5708
    c: Tangent(g42,g41) = -1.5708
    c: Tangent(g41,g43) = -1.5708
    c: Tangent(g43,g40) = -1.5708
    c: Equal(g40,g41)
    c: PointOnObject(g40,g39)
    c: PointOnObject(g41,g39)
    c: Tangent(g44,g46) = -1.5708
    c: Tangent(g46,g45) = -1.5708
    c: Tangent(g45,g47) = -1.5708
    c: Tangent(g47,g44) = -1.5708
    c: Equal(g44,g45)
    c: PointOnObject(g44,g39)
    c: PointOnObject(g45,g39)
    c: Tangent(g48,g50) = -1.5708
    c: Tangent(g50,g49) = -1.5708
    c: Tangent(g49,g51) = -1.5708
    c: Tangent(g51,g48) = -1.5708
    c: Equal(g48,g49)
    c: PointOnObject(g48,g39)
    c: Tangent(g52,g54) = -1.5708
    c: Tangent(g54,g53) = -1.5708
    c: Tangent(g53,g55) = -1.5708
    c: Tangent(g55,g52) = -1.5708
    c: Equal(g52,g53)
    c: PointOnObject(g52,g39)
    c: Equal(g31,g40)
    c: Equal(g40,g44)
    c: Equal(g44,g48)
    c: Equal(g48,g52)
    c: Symmetric(g39,g0,g-2)
    c: Equal(g33,g43)
    c: Equal(g43,g47)
    c: Equal(g47,g51)
    c: Equal(g51,g55)
    c: DistanceX(g6,g16) = 10
    c: DistanceX(g16,g21) = 10
    c: Equal(g0,g39)
    c: Symmetric(g39,g39,g56)
    c: Symmetric(g52,g53,g60)
    c: Symmetric(g49,g48,g59)
    c: Symmetric(g44,g45,g58)
    c: Symmetric(g41,g40,g57)
    c: Symmetric(g58,g59,g56)
    c: DistanceX(g58,g59) = 10
    c: DistanceX(g57,g58) = 10
    c: Symmetric(g57,g60,g56)
FEATURE [PartDesign::Pocket] Pocket010  label="TEK1_button"
  BaseFeature = -> Pocket008
  Direction = (0,0,-1)
  Length = 5
  Length2 = 5
  Profile = -> Sketch029
  ReferenceAxis = -> Sketch029 [N_Axis]
  Type = 0
FEATURE [TechDraw::DrawSVGTemplate] Template002
  Height = 210
  Orientation = 1
  Template = C:/Program Files/FreeCAD 0.21/data/Mod/TechDraw/Templates/A4_Landscape_blank.svg
  Width = 297
FEATURE [TechDraw::DrawViewAnnotation] Annotation002
  Font = osifont
  LineSpace = 100
  LockPosition = false
  MaxWidth = -1
  Rotation = 0
  ScaleType = 0
  Text = The mid of the datum plane A is preferred to be near | to the lower limit of the flatness tolerance zone. | It can be achieved with an additional bending step. | Aesthetical surfaces colored red on the view | No scratches, burrs or any kind of damage allowed! | Functional surfaces colored blue on the view (all which perpendicular to the aesthetical) | No burrs or other protruding material allowed!
  TextSize = 3
  TextStyle = 0
  X = 97.2718
  Y = 52.2376
FEATURE [TechDraw::DrawViewAnnotation] Annotation003
  Font = osifont
  LineSpace = 100
  LockPosition = false
  MaxWidth = -1
  Rotation = 0
  ScaleType = 0
  Text = The mid of the datum plane A is preferred to be near | to the lower limit of the flatness tolerance zone. | It can be achieved with an additional bending step.
  TextSize = 4
  TextStyle = 0
  X = 283.844
  Y = 84.5906
FEATURE [Sketcher::SketchObject] Sketch030  label="TEK2_ButtonHole001"
  FullyConstrained = true
  MapMode = 5
  Support = -> [XY_Plane011]
  sketch-geometry (97):
    g0: Circle CenterX=-40.005 CenterY=-13.335 CenterZ=0 NormalX=0 NormalY=0 NormalZ=1 AngleXU=0 Radius=2
    g1: Circle CenterX=-13.335 CenterY=-13.335 CenterZ=0 NormalX=0 NormalY=0 NormalZ=1 AngleXU=0 Radius=2
    g2: LineSegment StartX=-40.005 StartY=-13.335 StartZ=0 EndX=-13.335 EndY=-13.335 EndZ=0
    g3: Circle CenterX=13.335 CenterY=-13.335 CenterZ=0 NormalX=0 NormalY=0 NormalZ=1 AngleXU=0 Radius=2
    g4: LineSegment StartX=-13.335 StartY=-13.335 StartZ=0 EndX=13.335 EndY=-13.335 EndZ=0
    g5: Circle CenterX=40.005 CenterY=-13.335 CenterZ=0 NormalX=0 NormalY=0 NormalZ=1 AngleXU=0 Radius=2
    g6: LineSegment StartX=13.335 StartY=-13.335 StartZ=0 EndX=40.005 EndY=-13.335 EndZ=0
    g7: Circle CenterX=-40.005 CenterY=-40.005 CenterZ=0 NormalX=0 NormalY=0 NormalZ=1 AngleXU=0 Radius=2
    g8: LineSegment StartX=-40.005 StartY=-13.335 StartZ=0 EndX=-40.005 EndY=-40.005 EndZ=0
    g9: Circle CenterX=-13.335 CenterY=-40.005 CenterZ=0 NormalX=0 NormalY=0 NormalZ=1 AngleXU=0 Radius=2
    g10: LineSegment StartX=-40.005 StartY=-40.005 StartZ=0 EndX=-13.335 EndY=-40.005 EndZ=0
    g11: Circle CenterX=13.335 CenterY=-40.005 CenterZ=0 NormalX=0 NormalY=0 NormalZ=1 AngleXU=0 Radius=2
    g12: LineSegment StartX=-13.335 StartY=-40.005 StartZ=0 EndX=13.335 EndY=-40.005 EndZ=0
    g13: Circle CenterX=40.005 CenterY=-40.005 CenterZ=0 NormalX=0 NormalY=0 NormalZ=1 AngleXU=0 Radius=2
    g14: LineSegment StartX=13.335 StartY=-40.005 StartZ=0 EndX=40.005 EndY=-40.005 EndZ=0
    g15: LineSegment StartX=0 StartY=0 StartZ=0 EndX=13.335 EndY=-13.335 EndZ=0
    g16: LineSegment StartX=0 StartY=0 StartZ=0 EndX=-13.335 EndY=-13.335 EndZ=0
    g17: LineSegment StartX=-48.505 StartY=-19.735 StartZ=0 EndX=-48.505 EndY=-6.935 EndZ=0
    g18: LineSegment StartX=-46.405 StartY=-4.835 StartZ=0 EndX=-33.605 EndY=-4.835 EndZ=0
    g19: LineSegment StartX=-31.505 StartY=-6.935 StartZ=0 EndX=-31.505 EndY=-19.735 EndZ=0
    g20: LineSegment StartX=-33.605 StartY=-21.835 StartZ=0 EndX=-46.405 EndY=-21.835 EndZ=0
    g21: GeomPoint X=-40.005 Y=-13.335 Z=0
    g22: LineSegment StartX=-21.835 StartY=-19.735 StartZ=0 EndX=-21.835 EndY=-6.935 EndZ=0
    g23: LineSegment StartX=-19.735 StartY=-4.835 StartZ=0 EndX=-6.935 EndY=-4.835 EndZ=0
    g24: LineSegment StartX=-4.835 StartY=-6.935 StartZ=0 EndX=-4.835 EndY=-19.735 EndZ=0
    g25: LineSegment StartX=-6.935 StartY=-21.835 StartZ=0 EndX=-19.735 EndY=-21.835 EndZ=0
    g26: GeomPoint X=-13.335 Y=-13.335 Z=0
    g27: LineSegment StartX=4.835 StartY=-19.735 StartZ=0 EndX=4.835 EndY=-6.935 EndZ=0
    g28: LineSegment StartX=6.935 StartY=-4.835 StartZ=0 EndX=19.735 EndY=-4.835 EndZ=0
    g29: LineSegment StartX=21.835 StartY=-6.935 StartZ=0 EndX=21.835 EndY=-19.735 EndZ=0
    g30: LineSegment StartX=19.735 StartY=-21.835 StartZ=0 EndX=6.935 EndY=-21.835 EndZ=0
    g31: GeomPoint X=13.335 Y=-13.335 Z=0
    g32: LineSegment StartX=31.505 StartY=-19.735 StartZ=0 EndX=31.505 EndY=-6.935 EndZ=0
    g33: LineSegment StartX=33.605 StartY=-4.835 StartZ=0 EndX=46.405 EndY=-4.835 EndZ=0
    g34: LineSegment StartX=48.505 StartY=-6.935 StartZ=0 EndX=48.505 EndY=-19.735 EndZ=0
    g35: LineSegment StartX=46.405 StartY=-21.835 StartZ=0 EndX=33.605 EndY=-21.835 EndZ=0
    g36: GeomPoint X=40.005 Y=-13.335 Z=0
    g37: LineSegment StartX=31.505 StartY=-46.405 StartZ=0 EndX=31.505 EndY=-33.605 EndZ=0
    g38: LineSegment StartX=33.605 StartY=-31.505 StartZ=0 EndX=46.405 EndY=-31.505 EndZ=0
    g39: LineSegment StartX=48.505 StartY=-33.605 StartZ=0 EndX=48.505 EndY=-46.405 EndZ=0
    g40: LineSegment StartX=46.405 StartY=-48.505 StartZ=0 EndX=33.605 EndY=-48.505 EndZ=0
    g41: GeomPoint X=40.005 Y=-40.005 Z=0
    g42: LineSegment StartX=4.835 StartY=-46.405 StartZ=0 EndX=4.835 EndY=-33.605 EndZ=0
    g43: LineSegment StartX=6.935 StartY=-31.505 StartZ=0 EndX=19.735 EndY=-31.505 EndZ=0
    g44: LineSegment StartX=21.835 StartY=-33.605 StartZ=0 EndX=21.835 EndY=-46.405 EndZ=0
    g45: LineSegment StartX=19.735 StartY=-48.505 StartZ=0 EndX=6.935 EndY=-48.505 EndZ=0
    g46: GeomPoint X=13.335 Y=-40.005 Z=0
    g47: LineSegment StartX=-21.835 StartY=-46.405 StartZ=0 EndX=-21.835 EndY=-33.605 EndZ=0
    g48: LineSegment StartX=-19.735 StartY=-31.505 StartZ=0 EndX=-6.935 EndY=-31.505 EndZ=0
    g49: LineSegment StartX=-4.835 StartY=-33.605 StartZ=0 EndX=-4.835 EndY=-46.405 EndZ=0
    g50: LineSegment StartX=-6.935 StartY=-48.505 StartZ=0 EndX=-19.735 EndY=-48.505 EndZ=0
    g51: GeomPoint X=-13.335 Y=-40.005 Z=0
    g52: LineSegment StartX=-48.505 StartY=-46.405 StartZ=0 EndX=-48.505 EndY=-33.605 EndZ=0
    g53: LineSegment StartX=-46.405 StartY=-31.505 StartZ=0 EndX=-33.605 EndY=-31.505 EndZ=0
    g54: LineSegment StartX=-31.505 StartY=-33.605 StartZ=0 EndX=-31.505 EndY=-46.405 EndZ=0
    g55: LineSegment StartX=-33.605 StartY=-48.505 StartZ=0 EndX=-46.405 EndY=-48.505 EndZ=0
    g56: GeomPoint X=-40.005 Y=-40.005 Z=0
    g57: ArcOfCircle CenterX=-46.405 CenterY=-6.935 CenterZ=0 NormalX=0 NormalY=0 NormalZ=1 AngleXU=0 Radius=2.1 StartAngle=1.5708 EndAngle=3.14159
    g58: ArcOfCircle CenterX=-33.605 CenterY=-6.935 CenterZ=0 NormalX=0 NormalY=0 NormalZ=1 AngleXU=0 Radius=2.1 StartAngle=0 EndAngle=1.5708
    g59: ArcOfCircle CenterX=-33.605 CenterY=-19.735 CenterZ=0 NormalX=0 NormalY=0 NormalZ=1 AngleXU=0 Radius=2.1 StartAngle=4.71239 EndAngle=6.28319
    g60: ArcOfCircle CenterX=-46.405 CenterY=-19.735 CenterZ=0 NormalX=0 NormalY=0 NormalZ=1 AngleXU=0 Radius=2.1 StartAngle=3.14159 EndAngle=4.71239
    g61: ArcOfCircle CenterX=-19.735 CenterY=-6.935 CenterZ=0 NormalX=0 NormalY=0 NormalZ=1 AngleXU=0 Radius=2.1 StartAngle=1.5708 EndAngle=3.14159
    g62: ArcOfCircle CenterX=-19.735 CenterY=-19.735 CenterZ=0 NormalX=0 NormalY=0 NormalZ=1 AngleXU=0 Radius=2.1 StartAngle=3.14159 EndAngle=4.71239
    g63: ArcOfCircle CenterX=-6.935 CenterY=-19.735 CenterZ=0 NormalX=0 NormalY=0 NormalZ=1 AngleXU=0 Radius=2.1 StartAngle=4.71239 EndAngle=6.28319
    g64: ArcOfCircle CenterX=-6.935 CenterY=-6.935 CenterZ=0 NormalX=0 NormalY=0 NormalZ=1 AngleXU=0 Radius=2.1 StartAngle=0 EndAngle=1.5708
    g65: ArcOfCircle CenterX=6.935 CenterY=-6.935 CenterZ=0 NormalX=0 NormalY=0 NormalZ=1 AngleXU=0 Radius=2.1 StartAngle=1.5708 EndAngle=3.14159
    g66: ArcOfCircle CenterX=19.735 CenterY=-6.935 CenterZ=0 NormalX=0 NormalY=0 NormalZ=1 AngleXU=0 Radius=2.1 StartAngle=0 EndAngle=1.5708
    g67: ArcOfCircle CenterX=19.735 CenterY=-19.735 CenterZ=0 NormalX=0 NormalY=0 NormalZ=1 AngleXU=0 Radius=2.1 StartAngle=4.71239 EndAngle=6.28319
    g68: ArcOfCircle CenterX=6.935 CenterY=-19.735 CenterZ=0 NormalX=0 NormalY=0 NormalZ=1 AngleXU=0 Radius=2.1 StartAngle=3.14159 EndAngle=4.71239
    g69: ArcOfCircle CenterX=33.605 CenterY=-19.735 CenterZ=0 NormalX=0 NormalY=0 NormalZ=1 AngleXU=0 Radius=2.1 StartAngle=3.14159 EndAngle=4.71239
    g70: ArcOfCircle CenterX=46.405 CenterY=-6.935 CenterZ=0 NormalX=0 NormalY=0 NormalZ=1 AngleXU=0 Radius=2.1 StartAngle=0 EndAngle=1.5708
    g71: ArcOfCircle CenterX=33.605 CenterY=-6.935 CenterZ=0 NormalX=0 NormalY=0 NormalZ=1 AngleXU=0 Radius=2.1 StartAngle=1.5708 EndAngle=3.14159
    g72: ArcOfCircle CenterX=46.405 CenterY=-19.735 CenterZ=0 NormalX=0 NormalY=0 NormalZ=1 AngleXU=0 Radius=2.1 StartAngle=4.71239 EndAngle=6.28319
    g73: ArcOfCircle CenterX=33.605 CenterY=-33.605 CenterZ=0 NormalX=0 NormalY=0 NormalZ=1 AngleXU=0 Radius=2.1 StartAngle=1.5708 EndAngle=3.14159
    g74: ArcOfCircle CenterX=46.405 CenterY=-46.405 CenterZ=0 NormalX=0 NormalY=0 NormalZ=1 AngleXU=0 Radius=2.1 StartAngle=4.71239 EndAngle=6.28319
    g75: ArcOfCircle CenterX=46.405 CenterY=-33.605 CenterZ=0 NormalX=0 NormalY=0 NormalZ=1 AngleXU=0 Radius=2.1 StartAngle=-9e-16 EndAngle=1.5708
    g76: ArcOfCircle CenterX=33.605 CenterY=-46.405 CenterZ=0 NormalX=0 NormalY=0 NormalZ=1 AngleXU=0 Radius=2.1 StartAngle=3.14159 EndAngle=4.71239
    g77: ArcOfCircle CenterX=6.935 CenterY=-33.605 CenterZ=0 NormalX=0 NormalY=0 NormalZ=1 AngleXU=0 Radius=2.1 StartAngle=1.5708 EndAngle=3.14159
    g78: ArcOfCircle CenterX=19.735 CenterY=-33.605 CenterZ=0 NormalX=0 NormalY=0 NormalZ=1 AngleXU=0 Radius=2.1 StartAngle=-9e-16 EndAngle=1.5708
    g79: ArcOfCircle CenterX=19.735 CenterY=-46.405 CenterZ=0 NormalX=0 NormalY=0 NormalZ=1 AngleXU=0 Radius=2.1 StartAngle=4.71239 EndAngle=6.28319
    g80: ArcOfCircle CenterX=6.935 CenterY=-46.405 CenterZ=0 NormalX=0 NormalY=0 NormalZ=1 AngleXU=0 Radius=2.1 StartAngle=3.14159 EndAngle=4.71239
    g81: ArcOfCircle CenterX=-6.935 CenterY=-33.605 CenterZ=0 NormalX=0 NormalY=0 NormalZ=1 AngleXU=0 Radius=2.1 StartAngle=-1.8e-15 EndAngle=1.5708
    g82: ArcOfCircle CenterX=-19.735 CenterY=-46.405 CenterZ=0 NormalX=0 NormalY=0 NormalZ=1 AngleXU=0 Radius=2.1 StartAngle=3.14159 EndAngle=4.71239
    g83: ArcOfCircle CenterX=-19.735 CenterY=-33.605 CenterZ=0 NormalX=0 NormalY=0 NormalZ=1 AngleXU=0 Radius=2.1 StartAngle=1.5708 EndAngle=3.14159
    g84: ArcOfCircle CenterX=-6.935 CenterY=-46.405 CenterZ=0 NormalX=0 NormalY=0 NormalZ=1 AngleXU=0 Radius=2.1 StartAngle=4.71239 EndAngle=6.28319
    g85: ArcOfCircle CenterX=-46.405 CenterY=-33.605 CenterZ=0 NormalX=0 NormalY=0 NormalZ=1 AngleXU=0 Radius=2.1 StartAngle=1.5708 EndAngle=3.14159
    g86: ArcOfCircle CenterX=-33.605 CenterY=-33.605 CenterZ=0 NormalX=0 NormalY=0 NormalZ=1 AngleXU=0 Radius=2.1 StartAngle=-1.8e-15 EndAngle=1.5708
    g87: ArcOfCircle CenterX=-46.405 CenterY=-46.405 CenterZ=0 NormalX=0 NormalY=0 NormalZ=1 AngleXU=0 Radius=2.1 StartAngle=3.14159 EndAngle=4.71239
    g88: ArcOfCircle CenterX=-33.605 CenterY=-46.405 CenterZ=0 NormalX=0 NormalY=0 NormalZ=1 AngleXU=0 Radius=2.1 StartAngle=4.71239 EndAngle=6.28319
    g89: LineSegment StartX=-40.005 StartY=-4.835 StartZ=0 EndX=-40.005 EndY=-21.835 EndZ=0
    g90: LineSegment StartX=-13.335 StartY=-4.835 StartZ=0 EndX=-13.335 EndY=-21.835 EndZ=0
    g91: LineSegment StartX=13.335 StartY=-4.835 StartZ=0 EndX=13.335 EndY=-21.835 EndZ=0
    g92: LineSegment StartX=40.005 StartY=-4.835 StartZ=0 EndX=40.005 EndY=-21.835 EndZ=0
    g93: LineSegment StartX=40.005 StartY=-31.505 StartZ=0 EndX=40.005 EndY=-48.505 EndZ=0
    g94: LineSegment StartX=13.335 StartY=-31.505 StartZ=0 EndX=13.335 EndY=-48.505 EndZ=0
    g95: LineSegment StartX=-13.335 StartY=-31.505 StartZ=0 EndX=-13.335 EndY=-48.505 EndZ=0
    g96: LineSegment StartX=-40.005 StartY=-31.505 StartZ=0 EndX=-40.005 EndY=-48.505 EndZ=0
  constraints (226):
    c: Diameter(g0) = 4
    c: Coincident(g0,g2)
    c: Coincident(g1,g2)
    c: Coincident(g1,g4)
    c: Coincident(g3,g4)
    c: Coincident(g3,g6)
    c: Coincident(g5,g6)
    c: Coincident(g0,g8)
    c: Coincident(g7,g8)
    c: Coincident(g7,g10)
    c: Coincident(g9,g10)
    c: Coincident(g9,g12)
    c: Coincident(g11,g12)
    c: Coincident(g11,g14)
    c: Coincident(g13,g14)
    c: Coincident(g-1,g16)
    c: Coincident(g16,g1)
    c: Coincident(g15,g3)
    c: Horizontal(g4)
    c: Horizontal(g2)
    c: Horizontal(g6)
    c: Horizontal(g10)
    c: Horizontal(g12)
    c: Horizontal(g14)
    c: Vertical(g8)
    c: Equal(g8,g2)
    c: Equal(g2,g10)
    c: Equal(g10,g12)
    c: Equal(g12,g4)
    c: Equal(g4,g6)
    c: Equal(g6,g14)
    c: DistanceX(g4,g4) = 26.67
    c: Equal(g16,g15)
    c: Coincident(g15,g16)
    c: Perpendicular(g15,g16)
    c: Equal(g7,g9)
    c: Equal(g9,g11)
    c: Equal(g11,g13)
    c: Equal(g13,g5)
    c: Equal(g5,g3)
    c: Equal(g3,g1)
    c: Equal(g1,g0)
    c: Horizontal(g18)
    c: Horizontal(g20)
    c: Vertical(g17)
    c: Vertical(g19)
    c: Coincident(g21,g0)
    c: Horizontal(g23)
    c: Horizontal(g25)
    c: Vertical(g22)
    c: Vertical(g24)
    c: Coincident(g26,g1)
    c: Horizontal(g28)
    c: Horizontal(g30)
    c: Vertical(g27)
    c: Vertical(g29)
    c: Coincident(g31,g3)
    c: Horizontal(g33)
    c: Horizontal(g35)
    c: Vertical(g32)
    c: Vertical(g34)
    c: Coincident(g36,g5)
    c: Horizontal(g38)
    c: Horizontal(g40)
    c: Vertical(g37)
    c: Vertical(g39)
    c: Coincident(g41,g13)
    c: Horizontal(g43)
    c: Horizontal(g45)
    c: Vertical(g42)
    c: Vertical(g44)
    c: Coincident(g46,g11)
    c: Horizontal(g48)
    c: Horizontal(g50)
    c: Vertical(g47)
    c: Vertical(g49)
    c: Coincident(g51,g9)
    c: Horizontal(g53)
    c: Horizontal(g55)
    c: Vertical(g52)
    c: Vertical(g54)
    c: Coincident(g56,g7)
    c: Tangent(g18,g57) = 1.5708
    c: Tangent(g17,g57) = 1.5708
    c: Tangent(g18,g58) = 1.5708
    c: Tangent(g19,g58) = 1.5708
    c: Tangent(g19,g59) = 1.5708
    c: Tangent(g20,g59) = 1.5708
    c: Tangent(g20,g60) = 1.5708
    c: Tangent(g17,g60) = 1.5708
    c: Tangent(g23,g61) = 1.5708
    c: Tangent(g22,g61) = 1.5708
    c: Tangent(g22,g62) = 1.5708
    c: Tangent(g25,g62) = 1.5708
    c: Tangent(g24,g63) = 1.5708
    c: Tangent(g25,g63) = 1.5708
    c: Tangent(g23,g64) = 1.5708
    c: Tangent(g24,g64) = 1.5708
    c: Tangent(g27,g65) = 1.5708
    c: Tangent(g28,g65) = 1.5708
    c: Tangent(g28,g66) = 1.5708
    c: Tangent(g29,g66) = 1.5708
    c: Tangent(g29,g67) = 1.5708
    c: Tangent(g30,g67) = 1.5708
    c: Tangent(g27,g68) = 1.5708
    c: Tangent(g30,g68) = 1.5708
    c: Tangent(g32,g69) = 1.5708
    c: Tangent(g35,g69) = 1.5708
    c: Tangent(g33,g70) = 1.5708
    c: Tangent(g34,g70) = 1.5708
    c: Tangent(g33,g71) = 1.5708
    c: Tangent(g32,g71) = 1.5708
    c: Tangent(g34,g72) = 1.5708
    c: Tangent(g35,g72) = 1.5708
    c: Tangent(g38,g73) = 1.5708
    c: Tangent(g37,g73) = 1.5708
    c: Tangent(g39,g74) = 1.5708
    c: Tangent(g40,g74) = 1.5708
    c: Tangent(g38,g75) = 1.5708
    c: Tangent(g39,g75) = 1.5708
    c: Tangent(g37,g76) = 1.5708
    c: Tangent(g40,g76) = 1.5708
    c: Tangent(g43,g77) = 1.5708
    c: Tangent(g42,g77) = 1.5708
    c: Tangent(g43,g78) = 1.5708
    c: Tangent(g44,g78) = 1.5708
    c: Tangent(g44,g79) = 1.5708
    c: Tangent(g45,g79) = 1.5708
    c: Tangent(g42,g80) = 1.5708
    c: Tangent(g45,g80) = 1.5708
    c: Tangent(g48,g81) = 1.5708
    c: Tangent(g49,g81) = 1.5708
    c: Tangent(g47,g82) = 1.5708
    c: Tangent(g50,g82) = 1.5708
    c: Tangent(g47,g83) = 1.5708
    c: Tangent(g48,g83) = 1.5708
    c: Tangent(g49,g84) = 1.5708
    c: Tangent(g50,g84) = 1.5708
    c: Tangent(g53,g85) = 1.5708
    c: Tangent(g52,g85) = 1.5708
    c: Tangent(g53,g86) = 1.5708
    c: Tangent(g54,g86) = 1.5708
    c: Tangent(g55,g87) = 1.5708
    c: Tangent(g52,g87) = 1.5708
    c: Tangent(g54,g88) = 1.5708
    c: Tangent(g55,g88) = 1.5708
    c: Equal(g57,g58)
    c: Equal(g58,g59)
    c: Equal(g59,g60)
    c: Equal(g60,g85)
    c: Equal(g85,g86)
    c: Equal(g86,g88)
    c: Equal(g88,g87)
    c: Equal(g87,g61)
    c: Equal(g61,g64)
    c: Equal(g64,g63)
    c: Equal(g63,g62)
    c: Equal(g62,g68)
    c: Equal(g68,g67)
    c: Equal(g67,g65)
    c: Equal(g65,g66)
    c: Equal(g66,g71)
    c: Equal(g71,g70)
    c: Equal(g70,g72)
    c: Equal(g72,g69)
    c: Equal(g69,g73)
    c: Equal(g73,g75)
    c: Equal(g75,g74)
    c: Equal(g74,g76)
    c: Equal(g76,g78)
    c: Equal(g78,g77)
    c: Equal(g77,g80)
    c: Equal(g80,g79)
    c: Equal(g79,g81)
    c: Equal(g81,g83)
    c: Equal(g83,g82)
    c: Equal(g82,g84)
    c: Equal(g20,g19)
    c: Diameter(g57) = 4.2
    c: Equal(g40,g39)
    c: Equal(g39,g45)
    c: Equal(g45,g44)
    c: Equal(g44,g50)
    c: Equal(g50,g49)
    c: Equal(g49,g55)
    c: Equal(g55,g54)
    c: PointOnObject(g89,g20)
    c: Vertical(g89)
    c: DistanceY(g20,g18) = 17
    c: Symmetric(g18,g18,g89)
    c: PointOnObject(g90,g25)
    c: Vertical(g90)
    c: PointOnObject(g91,g30)
    c: Vertical(g91)
    c: PointOnObject(g92,g35)
    c: PointOnObject(g93,g40)
    c: PointOnObject(g94,g45)
    c: Vertical(g94)
    c: PointOnObject(g95,g50)
    c: PointOnObject(g96,g55)
    c: Vertical(g96)
    c: Symmetric(g23,g23,g90)
    c: Symmetric(g28,g28,g91)
    c: Vertical(g92)
    c: Symmetric(g33,g33,g92)
    c: Vertical(g93)
    c: Symmetric(g38,g38,g93)
    c: Symmetric(g43,g43,g94)
    c: Vertical(g95)
    c: Symmetric(g48,g48,g95)
    c: Symmetric(g53,g53,g96)
    c: Equal(g20,g25)
    c: Equal(g25,g24)
    c: Equal(g24,g30)
    c: Equal(g30,g29)
    c: Equal(g29,g35)
    c: Equal(g35,g34)
    c: Equal(g34,g55)
    c: Symmetric(g96,g96,g7)
    c: Symmetric(g95,g95,g9)
    c: Symmetric(g94,g94,g11)
    c: Symmetric(g93,g93,g13)
    c: Symmetric(g92,g92,g5)
    c: Symmetric(g91,g91,g3)
    c: Symmetric(g90,g90,g1)
    c: Symmetric(g89,g89,g0)
FEATURE [PartDesign::Pocket] Pocket011  label="TEK2_ButtonHole002"
  BaseFeature = -> Pocket010
  Direction = (0,0,-1)
  Length = 5
  Length2 = 5
  Profile = -> Sketch030
  ReferenceAxis = -> Sketch030 [N_Axis]
  Type = 1
FEATURE [PartDesign::Body] Body011  label="FRONTPANEL-SHEET-VSN2"
  BaseFeature = -> Body
  Group = -> [Clone009,Sketch023,Sketch024,Sketch025,Sketch026,Sketch027,Pocket008,Sketch028,Sketch029,Pocket010,Sketch030,Pocket011]
  Origin = -> Origin011
  Tip = -> Pocket011
FEATURE [TechDraw::DrawViewPart] View
  CoarseView = false
  Direction = (0,0,1)
  Focus = 100
  HardHidden = true
  IsoCount = 0
  IsoHidden = false
  IsoVisible = false
  LockPosition = false
  Perspective = false
  Rotation = 0
  ScaleType = 0
  ScrubCount = 0
  SeamHidden = false
  SeamVisible = true
  SmoothHidden = false
  SmoothVisible = true
  Source = -> [Body011]
  X = 123.684
  XDirection = (1,0,0)
  Y = 197.398
FEATURE [TechDraw::DrawViewPart] View001
  CoarseView = false
  Direction = (-1,0,0)
  Focus = 100
  HardHidden = true
  IsoCount = 0
  IsoHidden = false
  IsoVisible = false
  LockPosition = false
  Perspective = false
  Rotation = 0
  ScaleType = 0
  ScrubCount = 0
  SeamHidden = false
  SeamVisible = true
  SmoothHidden = false
  SmoothVisible = true
  Source = -> [Body011]
  X = 217.392
  XDirection = (0,0,1)
  Y = 197.186
FEATURE [TechDraw::DrawViewPart] View002
  CoarseView = false
  Direction = (0,0,-1)
  Focus = 100
  HardHidden = true
  IsoCount = 0
  IsoHidden = false
  IsoVisible = false
  LockPosition = false
  Perspective = false
  Rotation = 0
  ScaleType = 0
  ScrubCount = 0
  SeamHidden = false
  SeamVisible = true
  SmoothHidden = false
  SmoothVisible = true
  Source = -> [Body011]
  X = 309.133
  XDirection = (-1,0,0)
  Y = 197.302
FEATURE [TechDraw::DrawViewDimension] Dimension
  AngleOverride = false
  Arbitrary = false
  ArbitraryTolerances = false
  EqualTolerance = false
  ExtensionAngle = 0
  FormatSpec = %.2w
  FormatSpecOverTolerance = %+.2w
  FormatSpecUnderTolerance = %+.2w
  Inverted = false
  LineAngle = 0
  LockPosition = false
  MeasureType = 1
  OverTolerance = 0
  References2D = -> [View]
  Rotation = 0
  ScaleType = 0
  TheoreticalExact = false
  Type = 2
  UnderTolerance = -0.2
  X = 61.7953
  Y = 1.34438
FEATURE [TechDraw::DrawViewBalloon] Balloon
  BubbleShape = 6
  EndType = 6
  EndTypeScale = 1
  KinkLength = 0
  LockPosition = false
  OriginX = 70.4982
  OriginY = 52.3109
  Rotation = 0
  ScaleType = 0
  ShapeScale = 1
  SourceView = -> Dimension
  Text = C
  TextWrapLen = -1
  X = 70.6756
  Y = 62.9547
FEATURE [TechDraw::DrawViewBalloon] Balloon002
  BubbleShape = 6
  EndType = 0
  EndTypeScale = 1
  KinkLength = -0.1
  LockPosition = false
  OriginX = 0.5
  OriginY = 0
  Rotation = 0
  ScaleType = 0
  ShapeScale = 1
  SourceView = -> View001
  Text = ⏥|0.2
  TextWrapLen = -1
  X = 19.0698
  Y = 0.107397
FEATURE [TechDraw::DrawViewBalloon] Balloon003
  BubbleShape = 6
  EndType = 6
  EndTypeScale = 1
  KinkLength = -0.1
  LockPosition = false
  OriginX = 0.672888
  OriginY = 39.7383
  Rotation = 0
  ScaleType = 0
  ShapeScale = 1
  SourceView = -> View001
  Text = A
  TextWrapLen = -1
  X = 10.7916
  Y = 39.8457
FEATURE [TechDraw::DrawViewBalloon] Balloon008
  BubbleShape = 1
  EndType = 0
  EndTypeScale = 1
  KinkLength = -0.1
  LockPosition = false
  OriginX = -52.0652
  OriginY = 52.0652
  Rotation = 0
  ScaleType = 0
  ShapeScale = 1
  SourceView = -> View
  Text = 4× R0.38
  TextWrapLen = -1
  X = -75.4388
  Y = 68.3556
FEATURE [TechDraw::DrawComplexSection] ComplexSection  label="Section A - A"
  BaseView = -> View
  Caption = Section A-A
  CoarseView = false
  CutSurfaceDisplay = 2
  CuttingToolWireObject = -> Sketch026
  Direction = (1e-16,-1,0)
  FileGeomPattern = C:/Program Files/FreeCAD 0.21/data/Mod/TechDraw/PAT/FCPAT.pat
  FileHatchPattern = C:/Program Files/FreeCAD 0.21/data/Mod/TechDraw/Patterns/simple.svg
  Focus = 100
  FuseBeforeCut = false
  HardHidden = true
  HatchOffset = (0,0,0)
  HatchRotation = 0
  HatchScale = 1
  IsoCount = 0
  IsoHidden = false
  IsoVisible = false
  LockPosition = false
  NameGeomPattern = Gyémánt bevonatú
  Perspective = false
  ProjectionStrategy = 1
  Rotation = 0
  Scale = 10
  ScaleType = 2
  ScrubCount = 0
  SeamHidden = false
  SeamVisible = true
  SectionDirection = 4
  SectionNormal = (1e-16,-1,0)
  SectionOrigin = (0,0,0)
  SectionSymbol = A
  SmoothHidden = false
  SmoothVisible = true
  Source = -> [Body011]
  TrimAfterCut = false
  X = 287.429
  XDirection = (1,1e-16,0)
  Y = 98.2237
FEATURE [TechDraw::DrawViewDimension] Dimension008
  AngleOverride = false
  Arbitrary = false
  ArbitraryTolerances = false
  EqualTolerance = true
  ExtensionAngle = 0
  FormatSpec = 4x ⌀%.2w
  FormatSpecOverTolerance = %+.2w
  FormatSpecUnderTolerance = %+.2w
  Inverted = false
  LineAngle = 0
  LockPosition = false
  MeasureType = 1
  OverTolerance = 0
  References2D = -> [ComplexSection]
  Rotation = 0
  ScaleType = 0
  TheoreticalExact = false
  Type = 1
  UnderTolerance = 0
  X = 25.5096
  Y = 18.3127
FEATURE [TechDraw::DrawViewDimension] Dimension009
  AngleOverride = false
  Arbitrary = false
  ArbitraryTolerances = false
  EqualTolerance = true
  ExtensionAngle = 0
  FormatSpec = 4x ⌀%.2w
  FormatSpecOverTolerance = %+.2w
  FormatSpecUnderTolerance = %+.2w
  Inverted = false
  LineAngle = 0
  LockPosition = false
  MeasureType = 1
  OverTolerance = 0.05
  References2D = -> [ComplexSection]
  Rotation = 0
  ScaleType = 0
  TheoreticalExact = false
  Type = 1
  UnderTolerance = -0.05
  X = 48.7908
  Y = -4.80347
FEATURE [TechDraw::DrawViewBalloon] Balloon012
  BubbleShape = 6
  EndType = 6
  EndTypeScale = 1
  KinkLength = 0
  LockPosition = false
  OriginX = 46.1954
  OriginY = -17.0078
  Rotation = 0
  ScaleType = 0
  ShapeScale = 1
  SourceView = -> Dimension009
  Text = ⌖|⌀ 0.15|A|B|C
  TextWrapLen = -1
  X = 60.6339
  Y = -15.8915
FEATURE [TechDraw::DrawViewDimension] Dimension010
  AngleOverride = false
  Arbitrary = false
  ArbitraryTolerances = false
  EqualTolerance = true
  ExtensionAngle = 0
  FormatSpec = (%.2w)
  FormatSpecOverTolerance = %+.2w
  FormatSpecUnderTolerance = %+.2w
  Inverted = false
  LineAngle = 0
  LockPosition = false
  MeasureType = 1
  OverTolerance = 0
  References2D = -> [ComplexSection]
  Rotation = 0
  ScaleType = 0
  TheoreticalExact = false
  Type = 2
  UnderTolerance = 0
  X = -36.693
  Y = 2
FEATURE [TechDraw::DrawViewPart] View003
  CoarseView = false
  Direction = (0.57735,0.57735,0.57735)
  Focus = 100
  HardHidden = true
  IsoCount = 0
  IsoHidden = false
  IsoVisible = false
  LockPosition = false
  Perspective = false
  Rotation = 0
  Scale = 0.5
  ScaleType = 2
  ScrubCount = 0
  SeamHidden = false
  SeamVisible = true
  SmoothHidden = false
  SmoothVisible = true
  Source = -> [Body011]
  X = 195.909
  XDirection = (0.707107,0,-0.707107)
  Y = 92.6714
FEATURE [TechDraw::DrawHatch] Hatch  label="HatchF1"
  HatchPattern = C:/Program Files/FreeCAD 0.21/data/Mod/TechDraw/Patterns/solid.svg
  Source = -> View003 [Face1]
FEATURE [TechDraw::DrawViewBalloon] Balloon013
  BubbleShape = 1
  EndType = 3
  EndTypeScale = 1
  KinkLength = -0.1
  LockPosition = false
  OriginX = -18.2151
  OriginY = -14.1288
  Rotation = 0
  ScaleType = 0
  ShapeScale = 1
  SourceView = -> View003
  TextWrapLen = -1
  X = -91.3723
  Y = -74.5849
FEATURE [TechDraw::DrawViewDimension] Dimension017
  AngleOverride = false
  Arbitrary = false
  ArbitraryTolerances = false
  EqualTolerance = true
  ExtensionAngle = 0
  FormatSpec = 2× 4× R%.2w
  FormatSpecOverTolerance = %+.2w
  FormatSpecUnderTolerance = %+.2w
  Inverted = false
  LineAngle = 0
  LockPosition = false
  MeasureType = 1
  OverTolerance = 0
  References2D = -> [View002]
  Rotation = 0
  ScaleType = 0
  TheoreticalExact = false
  Type = 4
  UnderTolerance = 0
  X = 78.9859
  Y = 58.3117
FEATURE [TechDraw::DrawViewDimension] Dimension018
  AngleOverride = false
  Arbitrary = false
  ArbitraryTolerances = false
  EqualTolerance = true
  ExtensionAngle = 0
  FormatSpec = ⌀%.2w
  FormatSpecOverTolerance = %+.2w
  FormatSpecUnderTolerance = %+.2w
  Inverted = false
  LineAngle = 0
  LockPosition = false
  MeasureType = 1
  OverTolerance = 0
  References2D = -> [View002]
  Rotation = 0
  ScaleType = 0
  TheoreticalExact = false
  Type = 5
  UnderTolerance = 0
  X = 66.0837
  Y = 9.38895
FEATURE [TechDraw::DrawViewBalloon] Balloon018
  BubbleShape = 6
  EndType = 6
  EndTypeScale = 1
  KinkLength = 0
  LockPosition = false
  OriginX = 66.2827
  OriginY = 1.406
  Rotation = 0
  ScaleType = 0
  ShapeScale = 1
  SourceView = -> Dimension018
  Text = ⌖|⌀ 0,15|A|B|C
  TextWrapLen = -1
  X = 84.6059
  Y = -3.80857
FEATURE [TechDraw::DrawViewPart] View004
  CoarseView = false
  Direction = (0,0,1)
  Focus = 100
  HardHidden = false
  IsoCount = 0
  IsoHidden = false
  IsoVisible = true
  LockPosition = false
  Perspective = false
  Rotation = 0
  ScaleType = 0
  ScrubCount = 0
  SeamHidden = false
  SeamVisible = true
  SmoothHidden = false
  SmoothVisible = true
  Source = -> [Body011]
  X = 148.5
  XDirection = (1,3e-06,0)
  Y = 105
FEATURE [TechDraw::DrawPage] Page002  label="FRONTPANEL-SHEET-VSN2_dxf"
  KeepUpdated = true
  NextBalloonIndex = 1
  ProjectionType = 0
  Template = -> Template002
  Views = -> [View004]
FEATURE [TechDraw::DrawViewDimension] Dimension020
  AngleOverride = false
  Arbitrary = false
  ArbitraryTolerances = false
  EqualTolerance = true
  ExtensionAngle = 0
  FormatSpec = 4× 2× R%.2w
  FormatSpecOverTolerance = %+.2w
  FormatSpecUnderTolerance = %+.2w
  Inverted = false
  LineAngle = 0
  LockPosition = false
  MeasureType = 1
  OverTolerance = 0
  References2D = -> [View002]
  Rotation = 0
  ScaleType = 0
  TheoreticalExact = false
  Type = 4
  UnderTolerance = 0
  X = 78.3589
  Y = -15.5904
FEATURE [TechDraw::DrawHatch] Hatch001  label="Hatch001F65"
  HatchPattern = C:/Program Files/FreeCAD 0.21/data/Mod/TechDraw/Patterns/solid.svg
  Source = -> View003 [Face30]
FEATURE [TechDraw::DrawHatch] Hatch002  label="Hatch002F104"
  HatchPattern = C:/Program Files/FreeCAD 0.21/data/Mod/TechDraw/Patterns/solid.svg
  Source = -> View003 [Face32,Face33]
FEATURE [TechDraw::DrawHatch] Hatch003  label="Hatch003F68"
  HatchPattern = C:/Program Files/FreeCAD 0.21/data/Mod/TechDraw/Patterns/solid.svg
  Source = -> View003 [Face34,Face31,Face35]
FEATURE [TechDraw::DrawViewBalloon] Balloon023
  BubbleShape = 1
  EndType = 0
  EndTypeScale = 1
  KinkLength = 7
  LockPosition = false
  OriginX = 44.67
  OriginY = 4.77
  Rotation = 0
  ScaleType = 0
  ShapeScale = 1
  SourceView = -> View002
  Text = 8× 3×6
  TextWrapLen = -1
  X = 80.9138
  Y = -9.03731
FEATURE [TechDraw::DrawViewDimension] Dimension023
  AngleOverride = false
  Arbitrary = false
  ArbitraryTolerances = false
  EqualTolerance = true
  ExtensionAngle = 0
  FormatSpec = %.2w
  FormatSpecOverTolerance = %+.2w
  FormatSpecUnderTolerance = %+.2w
  Inverted = false
  LineAngle = 0
  LockPosition = false
  MeasureType = 1
  OverTolerance = 0
  References2D = -> [ComplexSection]
  Rotation = 0
  ScaleType = 0
  TheoreticalExact = false
  Type = 6
  UnderTolerance = 0
  X = -23.5911
  Y = 26.6553
FEATURE [TechDraw::DrawHatch] Hatch004  label="Hatch004F5"
  HatchPattern = C:/Program Files/FreeCAD 0.21/data/Mod/TechDraw/Patterns/solid.svg
  Source = -> View003 [Face5,Face4]
FEATURE [TechDraw::DrawHatch] Hatch005  label="Hatch005F22"
  HatchPattern = C:/Program Files/FreeCAD 0.21/data/Mod/TechDraw/Patterns/solid.svg
  Source = -> View003 [Face22,Face64,Face118,Face23,Face67,Face65,Face66]
FEATURE [TechDraw::DrawHatch] Hatch006  label="Hatch006F71"
  HatchPattern = C:/Program Files/FreeCAD 0.21/data/Mod/TechDraw/Patterns/solid.svg
  Source = -> View003 [Face71,Face37,Face106,Face50,Face98,Face41,Face68,Face45,Face107,Face103,Face40,Face75,Face39,Face105,Face112]
FEATURE [TechDraw::DrawHatch] Hatch007  label="Hatch007F69"
  HatchPattern = C:/Program Files/FreeCAD 0.21/data/Mod/TechDraw/Patterns/solid.svg
  Source = -> View003 [Face69,Face48,Face46,Face113,Face109,Face51,Face74,Face47,Face110,Face100,Face49,Face44,Face70,Face99,Face108,Face42,Face72,Face38,Face101,Face102,Face43,Face73,Face36,Face111,Edge297]
FEATURE [TechDraw::DrawHatch] Hatch008  label="Hatch008F104"
  HatchPattern = C:/Program Files/FreeCAD 0.21/data/Mod/TechDraw/Patterns/solid.svg
  Source = -> View003 [Face104,Face117,Face27,Face77,Face24,Face116,Face26,Face115,Face25,Face76,Face114]
FEATURE [TechDraw::DrawHatch] Hatch009  label="Hatch009F78"
  HatchPattern = C:/Program Files/FreeCAD 0.21/data/Mod/TechDraw/Patterns/solid.svg
  Source = -> View003 [Face78,Face88,Face125,Face79,Face87,Face126,Face81,Face86,Face130,Face84,Face89,Face128,Face83,Face90,Face127,Face85,Face91,Face129,Face82,Face92,Face123,Face80,Face93,Face124]
FEATURE [TechDraw::DrawViewDimension] Dimension024
  AngleOverride = false
  Arbitrary = false
  ArbitraryTolerances = false
  EqualTolerance = true
  ExtensionAngle = 0
  FormatSpec = 2× %.2w
  FormatSpecOverTolerance = %+.2w
  FormatSpecUnderTolerance = %+.2w
  Inverted = false
  LineAngle = 0
  LockPosition = false
  MeasureType = 1
  OverTolerance = 0
  References2D = -> [View002]
  Rotation = 0
  ScaleType = 0
  TheoreticalExact = false
  Type = 1
  UnderTolerance = 0
  X = 26.4692
  Y = 69.7683
FEATURE [TechDraw::DrawViewDimension] Dimension025
  AngleOverride = false
  Arbitrary = false
  ArbitraryTolerances = false
  EqualTolerance = true
  ExtensionAngle = 0
  FormatSpec = 2× %.2w
  FormatSpecOverTolerance = %+.2w
  FormatSpecUnderTolerance = %+.2w
  Inverted = false
  LineAngle = 0
  LockPosition = false
  MeasureType = 1
  OverTolerance = 0
  References2D = -> [View002]
  Rotation = 0
  ScaleType = 0
  TheoreticalExact = false
  Type = 2
  UnderTolerance = 0
  X = 70.6598
  Y = 27.4654
FEATURE [TechDraw::DrawViewBalloon] Balloon024
  BubbleShape = 6
  EndType = 0
  EndTypeScale = 1
  KinkLength = 5
  LockPosition = false
  OriginX = -26.67
  OriginY = 44.07
  Rotation = 0
  ScaleType = 0
  ShapeScale = 1
  SourceView = -> View
  Text = ⌓|0.2|A|B|C
  TextWrapLen = -1
  X = 18.0244
  Y = 68.2861
FEATURE [TechDraw::DrawViewAnnotation] Annotation004
  Font = osifont
  LineSpace = 100
  LockPosition = false
  MaxWidth = -1
  Rotation = 0
  ScaleType = 0
  Text = 2x
  TextSize = 4
  TextStyle = 0
  X = 119.086
  Y = 276.386
FEATURE [TechDraw::DrawViewDimension] Dimension026
  AngleOverride = false
  Arbitrary = false
  ArbitraryTolerances = true
  EqualTolerance = false
  ExtensionAngle = 0
  FormatSpec = %.2w
  FormatSpecOverTolerance = +0
  FormatSpecUnderTolerance = -0.2
  Inverted = false
  LineAngle = 0
  LockPosition = false
  MeasureType = 1
  OverTolerance = 0
  References2D = -> [View002]
  Rotation = 0
  ScaleType = 0
  TheoreticalExact = false
  Type = 1
  UnderTolerance = 0
  X = 0.708315
  Y = -61.211
FEATURE [TechDraw::DrawViewBalloon] Balloon025
  BubbleShape = 6
  EndType = 6
  EndTypeScale = 1
  KinkLength = 0
  LockPosition = false
  OriginX = 52.1505
  OriginY = -68.4541
  Rotation = 0
  ScaleType = 0
  ShapeScale = 1
  SourceView = -> Dimension026
  Text = B
  TextWrapLen = -1
  X = 62.7295
  Y = -68.5072
FEATURE [TechDraw::DrawViewDimension] Dimension027
  AngleOverride = false
  Arbitrary = false
  ArbitraryTolerances = false
  EqualTolerance = true
  ExtensionAngle = 0
  FormatSpec = 8× %.2w
  FormatSpecOverTolerance = %+.2w
  FormatSpecUnderTolerance = %+.2w
  Inverted = false
  LineAngle = 0
  LockPosition = false
  MeasureType = 1
  OverTolerance = 0
  References2D = -> [View]
  Rotation = 0
  ScaleType = 0
  TheoreticalExact = false
  Type = 1
  UnderTolerance = 0
  X = -17.0519
  Y = -54.5927
FEATURE [TechDraw::DrawViewDimension] Dimension028
  AngleOverride = false
  Arbitrary = false
  ArbitraryTolerances = false
  EqualTolerance = true
  ExtensionAngle = 0
  FormatSpec = 8× %.2w
  FormatSpecOverTolerance = %+.2w
  FormatSpecUnderTolerance = %+.2w
  Inverted = false
  LineAngle = 0
  LockPosition = false
  MeasureType = 1
  OverTolerance = 0
  References2D = -> [View]
  Rotation = 0
  ScaleType = 0
  TheoreticalExact = false
  Type = 2
  UnderTolerance = 0
  X = -61.7485
  Y = -38.005
FEATURE [TechDraw::DrawViewDimension] Dimension029
  AngleOverride = false
  Arbitrary = false
  ArbitraryTolerances = false
  EqualTolerance = true
  ExtensionAngle = 0
  FormatSpec = 8× 4×R%.2w
  FormatSpecOverTolerance = %+.2w
  FormatSpecUnderTolerance = %+.2w
  Inverted = false
  LineAngle = 0
  LockPosition = false
  MeasureType = 1
  OverTolerance = 0
  References2D = -> [View]
  Rotation = 0
  ScaleType = 0
  TheoreticalExact = false
  Type = 4
  UnderTolerance = 0
  X = -76.6534
  Y = -13.9472
FEATURE [TechDraw::DrawViewBalloon] Balloon026
  BubbleShape = 6
  EndType = 0
  EndTypeScale = 1
  KinkLength = 5
  LockPosition = false
  OriginX = -48.355
  OriginY = -13.335
  Rotation = 0
  ScaleType = 0
  ShapeScale = 1
  SourceView = -> View
  Text = ⌓|0.2|A|B|C
  TextWrapLen = -1
  X = -86.491
  Y = 1.83618
FEATURE [TechDraw::DrawViewAnnotation] Annotation005
  Font = osifont
  LineSpace = 100
  LockPosition = false
  MaxWidth = -1
  Rotation = 0
  ScaleType = 0
  Text = 8x
  TextSize = 4
  TextStyle = 0
  X = 16.035
  Y = 211.233
FEATURE [TechDraw::DrawPage] Page  label="VSN2_Drawing"
  KeepUpdated = true
  NextBalloonIndex = 39
  ProjectionType = 0
  Template = -> Template
  Views = -> [View,View001,View002,Dimension,Balloon,Balloon002,Balloon003,Balloon008,ComplexSection,Dimension008,Dimension009,Balloon012,Dimension010,Annotation,View003,Balloon013,Annotation001,Dimension017,Dimension018,Balloon018,Dimension020,Annotation002,Balloon023,Dimension023,Dimension024,Dimension025,Balloon024,Annotation004,Dimension026,Balloon025,Dimension027,Dimension028,Dimension029,Balloon026,+1 more]
FEATURE [TechDraw::DrawHatch] Hatch010  label="Hatch010F20"
  HatchPattern = C:/Program Files/FreeCAD 0.21/data/Mod/TechDraw/Patterns/solid.svg
  Source = -> View003 [Face20,Face19,Face17,Face15,Face21,Face16,Face18,Face14]
